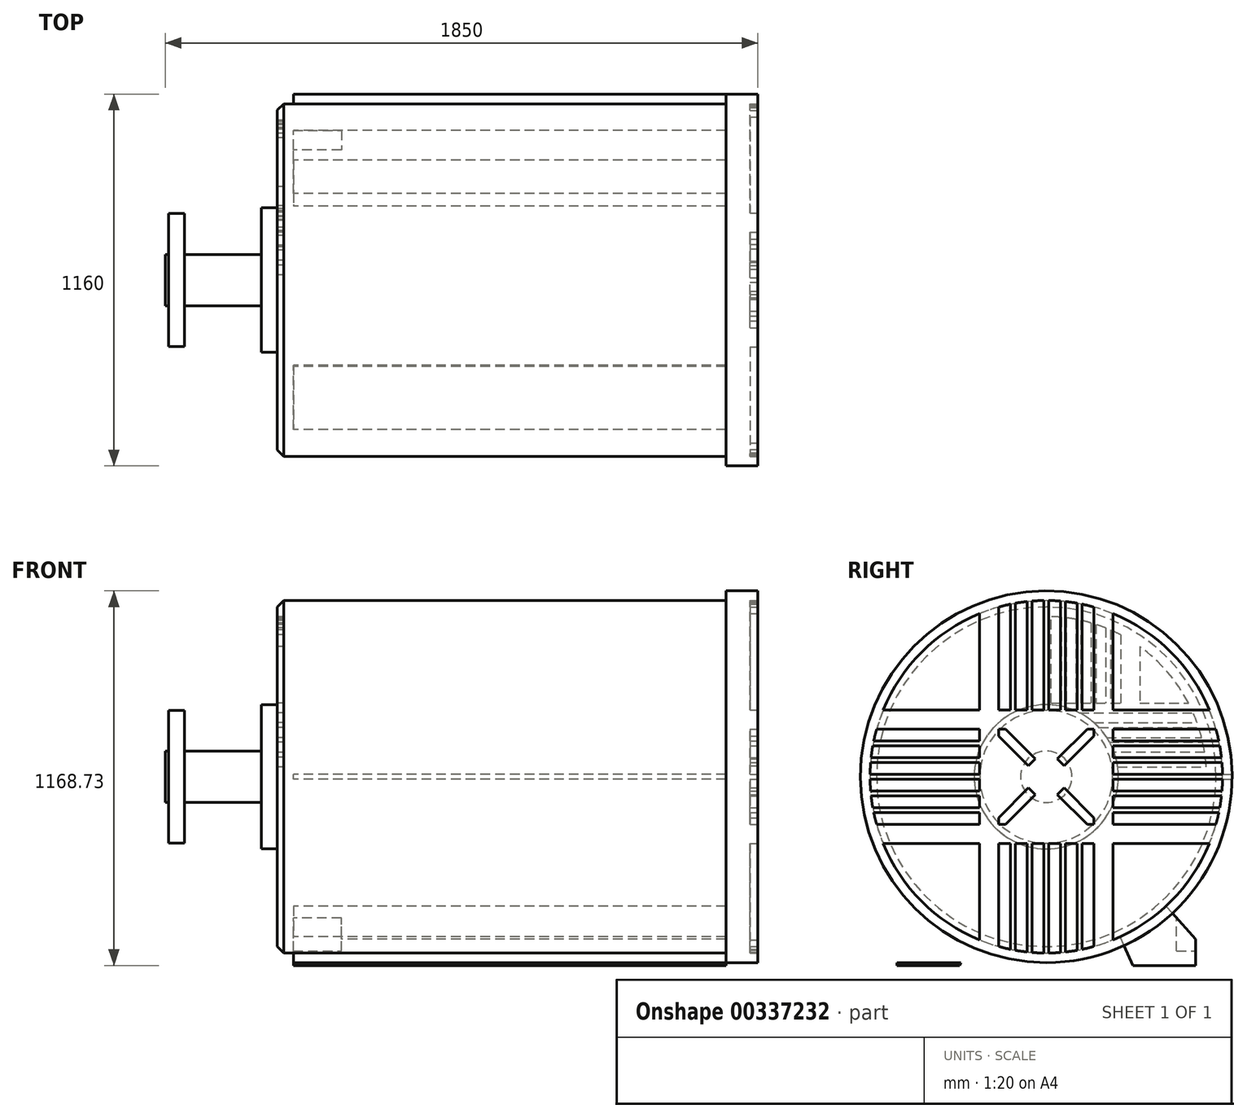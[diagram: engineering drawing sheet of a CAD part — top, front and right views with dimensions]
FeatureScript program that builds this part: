
annotation { "Feature Type Name" : "Feature", "Feature Type Description" : "" }
export const myFeature = defineFeature(function(context is Context, id is Id, definition is map)
    precondition{}
    {
        {
            var Q0;
            Q0=qCreatedBy(makeId("Right.planeOp"),FACE);
            var sketch = newSketch(context, id + "F0", { "sketchPlane" : qUnion([Q0])});
            skCircle(sketch, "E0", {"center": v(0, 0) * mm, "radius": 550 * mm});
            skSolve(sketch);
        }
        {
            var Q0;
            Q0=qSketchRegion(id+"F0",true);
            extrude(context, id + "F1", {"entities" : qUnion([Q0]), "depth" : 1350 * mm});
        }
        {
            var Q0;
            Q0=makeQuery(id+"F1.opExtrude","CAP_FACE",FACE,{"disambiguationData":[OSD([sQuery(id+"F0.wireOp",EDGE,"E0")])],"isStart":true});
            var sketch = newSketch(context, id + "F2", { "sketchPlane" : qUnion([Q0])});
            skLineSegment(sketch, "E1", {"start": v(0, 0) * mm, "end": v(-550, 0) * mm});
            skLineSegment(sketch, "E2", {"start": v(-549.95, 7.5) * mm, "end": v(-579.95, 7.5) * mm});
            skLineSegment(sketch, "E3", {"start": v(-549.95, -7.5) * mm, "end": v(-579.95, -7.5) * mm});
            skLineSegment(sketch, "E4", {"start": v(-549.95, 7.5) * mm, "end": v(-549.95, -7.5) * mm, "construction": true});
            skPoint(sketch, "E5", {"position": v(-549.95, 0) * mm});
            skArc(sketch, "E6", {"start": v(-579.95, 7.5) * mm, "mid": v(-580, 0) * mm, "end": v(-579.95, -7.5) * mm});
            skArc(sketch, "E7", {"start": v(-549.95, 7.5) * mm, "mid": v(-550, 0) * mm, "end": v(-549.95, -7.5) * mm});
            skSolve(sketch);
        }
        {
            var Q0;
            Q0=qSketchRegion(id+"F2",true);
            var Q1;
            Q1=makeQuery(id+"F1.opExtrude","CAP_FACE",FACE,{"disambiguationData":[OSD([sQuery(id+"F0.wireOp",EDGE,"E0")])],"isStart":false});
            extrude(context, id + "F3", {"entities" : qUnion([Q0]), "operationType" : NewBodyOperationType.ADD, "endBound" : BoundingType.UP_TO_SURFACE, "oppositeDirection" : true, "endBoundEntityFace" : qUnion([Q1]), "depth" : 25 * mm});
        }
        {
            var Q0;
            {var subQ0=sQuery(id+"F2.wireOp",EDGE,"E7");var subQ1=sQuery(id+"F2.wireOp",EDGE,"E6");var subQ2=sQuery(id+"F2.wireOp",EDGE,"E3");var subQ3=sQuery(id+"F2.wireOp",EDGE,"E2");Q0=makeQuery(id+"F7dXQ7x4IlYUw1S_1.59.F3.boolean.opBoolean","MERGE",FACE,{"derivedFrom":[makeQuery(id+"F7dXQ7x4IlYUw1S_1.58.F3.boolean.opBoolean","MERGE",FACE,{"derivedFrom":[makeQuery(id+"F7dXQ7x4IlYUw1S_1.57.F3.boolean.opBoolean","MERGE",FACE,{"derivedFrom":[makeQuery(id+"F7dXQ7x4IlYUw1S_1.56.F3.boolean.opBoolean","MERGE",FACE,{"derivedFrom":[makeQuery(id+"F7dXQ7x4IlYUw1S_1.55.F3.boolean.opBoolean","MERGE",FACE,{"derivedFrom":[makeQuery(id+"F7dXQ7x4IlYUw1S_1.54.F3.boolean.opBoolean","MERGE",FACE,{"derivedFrom":[makeQuery(id+"F7dXQ7x4IlYUw1S_1.53.F3.boolean.opBoolean","MERGE",FACE,{"derivedFrom":[makeQuery(id+"F7dXQ7x4IlYUw1S_1.52.F3.boolean.opBoolean","MERGE",FACE,{"derivedFrom":[makeQuery(id+"F7dXQ7x4IlYUw1S_1.51.F3.boolean.opBoolean","MERGE",FACE,{"derivedFrom":[makeQuery(id+"F7dXQ7x4IlYUw1S_1.50.F3.boolean.opBoolean","MERGE",FACE,{"derivedFrom":[makeQuery(id+"F7dXQ7x4IlYUw1S_1.49.F3.boolean.opBoolean","MERGE",FACE,{"derivedFrom":[makeQuery(id+"F7dXQ7x4IlYUw1S_1.48.F3.boolean.opBoolean","MERGE",FACE,{"derivedFrom":[makeQuery(id+"F7dXQ7x4IlYUw1S_1.47.F3.boolean.opBoolean","MERGE",FACE,{"derivedFrom":[makeQuery(id+"F7dXQ7x4IlYUw1S_1.46.F3.boolean.opBoolean","MERGE",FACE,{"derivedFrom":[makeQuery(id+"F7dXQ7x4IlYUw1S_1.45.F3.boolean.opBoolean","MERGE",FACE,{"derivedFrom":[makeQuery(id+"F7dXQ7x4IlYUw1S_1.44.F3.boolean.opBoolean","MERGE",FACE,{"derivedFrom":[makeQuery(id+"F7dXQ7x4IlYUw1S_1.43.F3.boolean.opBoolean","MERGE",FACE,{"derivedFrom":[makeQuery(id+"F7dXQ7x4IlYUw1S_1.42.F3.boolean.opBoolean","MERGE",FACE,{"derivedFrom":[makeQuery(id+"F7dXQ7x4IlYUw1S_1.41.F3.boolean.opBoolean","MERGE",FACE,{"derivedFrom":[makeQuery(id+"F7dXQ7x4IlYUw1S_1.40.F3.boolean.opBoolean","MERGE",FACE,{"derivedFrom":[makeQuery(id+"F7dXQ7x4IlYUw1S_1.39.F3.boolean.opBoolean","MERGE",FACE,{"derivedFrom":[makeQuery(id+"F7dXQ7x4IlYUw1S_1.38.F3.boolean.opBoolean","MERGE",FACE,{"derivedFrom":[makeQuery(id+"F7dXQ7x4IlYUw1S_1.37.F3.boolean.opBoolean","MERGE",FACE,{"derivedFrom":[makeQuery(id+"F7dXQ7x4IlYUw1S_1.36.F3.boolean.opBoolean","MERGE",FACE,{"derivedFrom":[makeQuery(id+"F7dXQ7x4IlYUw1S_1.35.F3.boolean.opBoolean","MERGE",FACE,{"derivedFrom":[makeQuery(id+"F7dXQ7x4IlYUw1S_1.34.F3.boolean.opBoolean","MERGE",FACE,{"derivedFrom":[makeQuery(id+"F7dXQ7x4IlYUw1S_1.33.F3.boolean.opBoolean","MERGE",FACE,{"derivedFrom":[makeQuery(id+"F7dXQ7x4IlYUw1S_1.32.F3.boolean.opBoolean","MERGE",FACE,{"derivedFrom":[makeQuery(id+"F7dXQ7x4IlYUw1S_1.31.F3.boolean.opBoolean","MERGE",FACE,{"derivedFrom":[makeQuery(id+"F7dXQ7x4IlYUw1S_1.30.F3.boolean.opBoolean","MERGE",FACE,{"derivedFrom":[makeQuery(id+"F7dXQ7x4IlYUw1S_1.29.F3.boolean.opBoolean","MERGE",FACE,{"derivedFrom":[makeQuery(id+"F7dXQ7x4IlYUw1S_1.28.F3.boolean.opBoolean","MERGE",FACE,{"derivedFrom":[makeQuery(id+"F7dXQ7x4IlYUw1S_1.27.F3.boolean.opBoolean","MERGE",FACE,{"derivedFrom":[makeQuery(id+"F7dXQ7x4IlYUw1S_1.26.F3.boolean.opBoolean","MERGE",FACE,{"derivedFrom":[makeQuery(id+"F7dXQ7x4IlYUw1S_1.25.F3.boolean.opBoolean","MERGE",FACE,{"derivedFrom":[makeQuery(id+"F7dXQ7x4IlYUw1S_1.24.F3.boolean.opBoolean","MERGE",FACE,{"derivedFrom":[makeQuery(id+"F7dXQ7x4IlYUw1S_1.23.F3.boolean.opBoolean","MERGE",FACE,{"derivedFrom":[makeQuery(id+"F7dXQ7x4IlYUw1S_1.22.F3.boolean.opBoolean","MERGE",FACE,{"derivedFrom":[makeQuery(id+"F7dXQ7x4IlYUw1S_1.21.F3.boolean.opBoolean","MERGE",FACE,{"derivedFrom":[makeQuery(id+"F7dXQ7x4IlYUw1S_1.20.F3.boolean.opBoolean","MERGE",FACE,{"derivedFrom":[makeQuery(id+"F7dXQ7x4IlYUw1S_1.19.F3.boolean.opBoolean","MERGE",FACE,{"derivedFrom":[makeQuery(id+"F7dXQ7x4IlYUw1S_1.18.F3.boolean.opBoolean","MERGE",FACE,{"derivedFrom":[makeQuery(id+"F7dXQ7x4IlYUw1S_1.17.F3.boolean.opBoolean","MERGE",FACE,{"derivedFrom":[makeQuery(id+"F7dXQ7x4IlYUw1S_1.16.F3.boolean.opBoolean","MERGE",FACE,{"derivedFrom":[makeQuery(id+"F7dXQ7x4IlYUw1S_1.15.F3.boolean.opBoolean","MERGE",FACE,{"derivedFrom":[makeQuery(id+"F7dXQ7x4IlYUw1S_1.14.F3.boolean.opBoolean","MERGE",FACE,{"derivedFrom":[makeQuery(id+"F7dXQ7x4IlYUw1S_1.13.F3.boolean.opBoolean","MERGE",FACE,{"derivedFrom":[makeQuery(id+"F7dXQ7x4IlYUw1S_1.12.F3.boolean.opBoolean","MERGE",FACE,{"derivedFrom":[makeQuery(id+"F7dXQ7x4IlYUw1S_1.11.F3.boolean.opBoolean","MERGE",FACE,{"derivedFrom":[makeQuery(id+"F7dXQ7x4IlYUw1S_1.10.F3.boolean.opBoolean","MERGE",FACE,{"derivedFrom":[makeQuery(id+"F7dXQ7x4IlYUw1S_1.9.F3.boolean.opBoolean","MERGE",FACE,{"derivedFrom":[makeQuery(id+"F7dXQ7x4IlYUw1S_1.8.F3.boolean.opBoolean","MERGE",FACE,{"derivedFrom":[makeQuery(id+"F7dXQ7x4IlYUw1S_1.7.F3.boolean.opBoolean","MERGE",FACE,{"derivedFrom":[makeQuery(id+"F7dXQ7x4IlYUw1S_1.6.F3.boolean.opBoolean","MERGE",FACE,{"derivedFrom":[makeQuery(id+"F7dXQ7x4IlYUw1S_1.5.F3.boolean.opBoolean","MERGE",FACE,{"derivedFrom":[makeQuery(id+"F7dXQ7x4IlYUw1S_1.4.F3.boolean.opBoolean","MERGE",FACE,{"derivedFrom":[makeQuery(id+"F7dXQ7x4IlYUw1S_1.3.F3.boolean.opBoolean","MERGE",FACE,{"derivedFrom":[makeQuery(id+"F7dXQ7x4IlYUw1S_1.2.F3.boolean.opBoolean","MERGE",FACE,{"derivedFrom":[makeQuery(id+"F7dXQ7x4IlYUw1S_1.1.F3.boolean.opBoolean","MERGE",FACE,{"derivedFrom":[makeQuery(id+"F3.boolean.opBoolean","MERGE",FACE,{"derivedFrom":[makeQuery(id+"F1.opExtrude","CAP_FACE",FACE,{"disambiguationData":[OSD([sQuery(id+"F0.wireOp",EDGE,"E0")])],"isStart":true}),makeQuery(id+"F3.opExtrude","CAP_FACE",FACE,{"disambiguationData":[OSD([subQ3,subQ2,subQ1,subQ0])],"isStart":true})]}),makeQuery(id+"F7dXQ7x4IlYUw1S_1.1.F3.opExtrude","CAP_FACE",FACE,{"disambiguationData":[OSD([subQ3,subQ2,subQ1,subQ0])],"isStart":true})]}),makeQuery(id+"F7dXQ7x4IlYUw1S_1.2.F3.opExtrude","CAP_FACE",FACE,{"disambiguationData":[OSD([subQ3,subQ2,subQ1,subQ0])],"isStart":true})]}),makeQuery(id+"F7dXQ7x4IlYUw1S_1.3.F3.opExtrude","CAP_FACE",FACE,{"disambiguationData":[OSD([subQ3,subQ2,subQ1,subQ0])],"isStart":true})]}),makeQuery(id+"F7dXQ7x4IlYUw1S_1.4.F3.opExtrude","CAP_FACE",FACE,{"disambiguationData":[OSD([subQ3,subQ2,subQ1,subQ0])],"isStart":true})]}),makeQuery(id+"F7dXQ7x4IlYUw1S_1.5.F3.opExtrude","CAP_FACE",FACE,{"disambiguationData":[OSD([subQ3,subQ2,subQ1,subQ0])],"isStart":true})]}),makeQuery(id+"F7dXQ7x4IlYUw1S_1.6.F3.opExtrude","CAP_FACE",FACE,{"disambiguationData":[OSD([subQ3,subQ2,subQ1,subQ0])],"isStart":true})]}),makeQuery(id+"F7dXQ7x4IlYUw1S_1.7.F3.opExtrude","CAP_FACE",FACE,{"disambiguationData":[OSD([subQ3,subQ2,subQ1,subQ0])],"isStart":true})]}),makeQuery(id+"F7dXQ7x4IlYUw1S_1.8.F3.opExtrude","CAP_FACE",FACE,{"disambiguationData":[OSD([subQ3,subQ2,subQ1,subQ0])],"isStart":true})]}),makeQuery(id+"F7dXQ7x4IlYUw1S_1.9.F3.opExtrude","CAP_FACE",FACE,{"disambiguationData":[OSD([subQ3,subQ2,subQ1,subQ0])],"isStart":true})]}),makeQuery(id+"F7dXQ7x4IlYUw1S_1.10.F3.opExtrude","CAP_FACE",FACE,{"disambiguationData":[OSD([subQ3,subQ2,subQ1,subQ0])],"isStart":true})]}),makeQuery(id+"F7dXQ7x4IlYUw1S_1.11.F3.opExtrude","CAP_FACE",FACE,{"disambiguationData":[OSD([subQ3,subQ2,subQ1,subQ0])],"isStart":true})]}),makeQuery(id+"F7dXQ7x4IlYUw1S_1.12.F3.opExtrude","CAP_FACE",FACE,{"disambiguationData":[OSD([subQ3,subQ2,subQ1,subQ0])],"isStart":true})]}),makeQuery(id+"F7dXQ7x4IlYUw1S_1.13.F3.opExtrude","CAP_FACE",FACE,{"disambiguationData":[OSD([subQ3,subQ2,subQ1,subQ0])],"isStart":true})]}),makeQuery(id+"F7dXQ7x4IlYUw1S_1.14.F3.opExtrude","CAP_FACE",FACE,{"disambiguationData":[OSD([subQ3,subQ2,subQ1,subQ0])],"isStart":true})]}),makeQuery(id+"F7dXQ7x4IlYUw1S_1.15.F3.opExtrude","CAP_FACE",FACE,{"disambiguationData":[OSD([subQ3,subQ2,subQ1,subQ0])],"isStart":true})]}),makeQuery(id+"F7dXQ7x4IlYUw1S_1.16.F3.opExtrude","CAP_FACE",FACE,{"disambiguationData":[OSD([subQ3,subQ2,subQ1,subQ0])],"isStart":true})]}),makeQuery(id+"F7dXQ7x4IlYUw1S_1.17.F3.opExtrude","CAP_FACE",FACE,{"disambiguationData":[OSD([subQ3,subQ2,subQ1,subQ0])],"isStart":true})]}),makeQuery(id+"F7dXQ7x4IlYUw1S_1.18.F3.opExtrude","CAP_FACE",FACE,{"disambiguationData":[OSD([subQ3,subQ2,subQ1,subQ0])],"isStart":true})]}),makeQuery(id+"F7dXQ7x4IlYUw1S_1.19.F3.opExtrude","CAP_FACE",FACE,{"disambiguationData":[OSD([subQ3,subQ2,subQ1,subQ0])],"isStart":true})]}),makeQuery(id+"F7dXQ7x4IlYUw1S_1.20.F3.opExtrude","CAP_FACE",FACE,{"disambiguationData":[OSD([subQ3,subQ2,subQ1,subQ0])],"isStart":true})]}),makeQuery(id+"F7dXQ7x4IlYUw1S_1.21.F3.opExtrude","CAP_FACE",FACE,{"disambiguationData":[OSD([subQ3,subQ2,subQ1,subQ0])],"isStart":true})]}),makeQuery(id+"F7dXQ7x4IlYUw1S_1.22.F3.opExtrude","CAP_FACE",FACE,{"disambiguationData":[OSD([subQ3,subQ2,subQ1,subQ0])],"isStart":true})]}),makeQuery(id+"F7dXQ7x4IlYUw1S_1.23.F3.opExtrude","CAP_FACE",FACE,{"disambiguationData":[OSD([subQ3,subQ2,subQ1,subQ0])],"isStart":true})]}),makeQuery(id+"F7dXQ7x4IlYUw1S_1.24.F3.opExtrude","CAP_FACE",FACE,{"disambiguationData":[OSD([subQ3,subQ2,subQ1,subQ0])],"isStart":true})]}),makeQuery(id+"F7dXQ7x4IlYUw1S_1.25.F3.opExtrude","CAP_FACE",FACE,{"disambiguationData":[OSD([subQ3,subQ2,subQ1,subQ0])],"isStart":true})]}),makeQuery(id+"F7dXQ7x4IlYUw1S_1.26.F3.opExtrude","CAP_FACE",FACE,{"disambiguationData":[OSD([subQ3,subQ2,subQ1,subQ0])],"isStart":true})]}),makeQuery(id+"F7dXQ7x4IlYUw1S_1.27.F3.opExtrude","CAP_FACE",FACE,{"disambiguationData":[OSD([subQ3,subQ2,subQ1,subQ0])],"isStart":true})]}),makeQuery(id+"F7dXQ7x4IlYUw1S_1.28.F3.opExtrude","CAP_FACE",FACE,{"disambiguationData":[OSD([subQ3,subQ2,subQ1,subQ0])],"isStart":true})]}),makeQuery(id+"F7dXQ7x4IlYUw1S_1.29.F3.opExtrude","CAP_FACE",FACE,{"disambiguationData":[OSD([subQ3,subQ2,subQ1,subQ0])],"isStart":true})]}),makeQuery(id+"F7dXQ7x4IlYUw1S_1.30.F3.opExtrude","CAP_FACE",FACE,{"disambiguationData":[OSD([subQ3,subQ2,subQ1,subQ0])],"isStart":true})]}),makeQuery(id+"F7dXQ7x4IlYUw1S_1.31.F3.opExtrude","CAP_FACE",FACE,{"disambiguationData":[OSD([subQ3,subQ2,subQ1,subQ0])],"isStart":true})]}),makeQuery(id+"F7dXQ7x4IlYUw1S_1.32.F3.opExtrude","CAP_FACE",FACE,{"disambiguationData":[OSD([subQ3,subQ2,subQ1,subQ0])],"isStart":true})]}),makeQuery(id+"F7dXQ7x4IlYUw1S_1.33.F3.opExtrude","CAP_FACE",FACE,{"disambiguationData":[OSD([subQ3,subQ2,subQ1,subQ0])],"isStart":true})]}),makeQuery(id+"F7dXQ7x4IlYUw1S_1.34.F3.opExtrude","CAP_FACE",FACE,{"disambiguationData":[OSD([subQ3,subQ2,subQ1,subQ0])],"isStart":true})]}),makeQuery(id+"F7dXQ7x4IlYUw1S_1.35.F3.opExtrude","CAP_FACE",FACE,{"disambiguationData":[OSD([subQ3,subQ2,subQ1,subQ0])],"isStart":true})]}),makeQuery(id+"F7dXQ7x4IlYUw1S_1.36.F3.opExtrude","CAP_FACE",FACE,{"disambiguationData":[OSD([subQ3,subQ2,subQ1,subQ0])],"isStart":true})]}),makeQuery(id+"F7dXQ7x4IlYUw1S_1.37.F3.opExtrude","CAP_FACE",FACE,{"disambiguationData":[OSD([subQ3,subQ2,subQ1,subQ0])],"isStart":true})]}),makeQuery(id+"F7dXQ7x4IlYUw1S_1.38.F3.opExtrude","CAP_FACE",FACE,{"disambiguationData":[OSD([subQ3,subQ2,subQ1,subQ0])],"isStart":true})]}),makeQuery(id+"F7dXQ7x4IlYUw1S_1.39.F3.opExtrude","CAP_FACE",FACE,{"disambiguationData":[OSD([subQ3,subQ2,subQ1,subQ0])],"isStart":true})]}),makeQuery(id+"F7dXQ7x4IlYUw1S_1.40.F3.opExtrude","CAP_FACE",FACE,{"disambiguationData":[OSD([subQ3,subQ2,subQ1,subQ0])],"isStart":true})]}),makeQuery(id+"F7dXQ7x4IlYUw1S_1.41.F3.opExtrude","CAP_FACE",FACE,{"disambiguationData":[OSD([subQ3,subQ2,subQ1,subQ0])],"isStart":true})]}),makeQuery(id+"F7dXQ7x4IlYUw1S_1.42.F3.opExtrude","CAP_FACE",FACE,{"disambiguationData":[OSD([subQ3,subQ2,subQ1,subQ0])],"isStart":true})]}),makeQuery(id+"F7dXQ7x4IlYUw1S_1.43.F3.opExtrude","CAP_FACE",FACE,{"disambiguationData":[OSD([subQ3,subQ2,subQ1,subQ0])],"isStart":true})]}),makeQuery(id+"F7dXQ7x4IlYUw1S_1.44.F3.opExtrude","CAP_FACE",FACE,{"disambiguationData":[OSD([subQ3,subQ2,subQ1,subQ0])],"isStart":true})]}),makeQuery(id+"F7dXQ7x4IlYUw1S_1.45.F3.opExtrude","CAP_FACE",FACE,{"disambiguationData":[OSD([subQ3,subQ2,subQ1,subQ0])],"isStart":true})]}),makeQuery(id+"F7dXQ7x4IlYUw1S_1.46.F3.opExtrude","CAP_FACE",FACE,{"disambiguationData":[OSD([subQ3,subQ2,subQ1,subQ0])],"isStart":true})]}),makeQuery(id+"F7dXQ7x4IlYUw1S_1.47.F3.opExtrude","CAP_FACE",FACE,{"disambiguationData":[OSD([subQ3,subQ2,subQ1,subQ0])],"isStart":true})]}),makeQuery(id+"F7dXQ7x4IlYUw1S_1.48.F3.opExtrude","CAP_FACE",FACE,{"disambiguationData":[OSD([subQ3,subQ2,subQ1,subQ0])],"isStart":true})]}),makeQuery(id+"F7dXQ7x4IlYUw1S_1.49.F3.opExtrude","CAP_FACE",FACE,{"disambiguationData":[OSD([subQ3,subQ2,subQ1,subQ0])],"isStart":true})]}),makeQuery(id+"F7dXQ7x4IlYUw1S_1.50.F3.opExtrude","CAP_FACE",FACE,{"disambiguationData":[OSD([subQ3,subQ2,subQ1,subQ0])],"isStart":true})]}),makeQuery(id+"F7dXQ7x4IlYUw1S_1.51.F3.opExtrude","CAP_FACE",FACE,{"disambiguationData":[OSD([subQ3,subQ2,subQ1,subQ0])],"isStart":true})]}),makeQuery(id+"F7dXQ7x4IlYUw1S_1.52.F3.opExtrude","CAP_FACE",FACE,{"disambiguationData":[OSD([subQ3,subQ2,subQ1,subQ0])],"isStart":true})]}),makeQuery(id+"F7dXQ7x4IlYUw1S_1.53.F3.opExtrude","CAP_FACE",FACE,{"disambiguationData":[OSD([subQ3,subQ2,subQ1,subQ0])],"isStart":true})]}),makeQuery(id+"F7dXQ7x4IlYUw1S_1.54.F3.opExtrude","CAP_FACE",FACE,{"disambiguationData":[OSD([subQ3,subQ2,subQ1,subQ0])],"isStart":true})]}),makeQuery(id+"F7dXQ7x4IlYUw1S_1.55.F3.opExtrude","CAP_FACE",FACE,{"disambiguationData":[OSD([subQ3,subQ2,subQ1,subQ0])],"isStart":true})]}),makeQuery(id+"F7dXQ7x4IlYUw1S_1.56.F3.opExtrude","CAP_FACE",FACE,{"disambiguationData":[OSD([subQ3,subQ2,subQ1,subQ0])],"isStart":true})]}),makeQuery(id+"F7dXQ7x4IlYUw1S_1.57.F3.opExtrude","CAP_FACE",FACE,{"disambiguationData":[OSD([subQ3,subQ2,subQ1,subQ0])],"isStart":true})]}),makeQuery(id+"F7dXQ7x4IlYUw1S_1.58.F3.opExtrude","CAP_FACE",FACE,{"disambiguationData":[OSD([subQ3,subQ2,subQ1,subQ0])],"isStart":true})]}),makeQuery(id+"F7dXQ7x4IlYUw1S_1.59.F3.opExtrude","CAP_FACE",FACE,{"disambiguationData":[OSD([subQ3,subQ2,subQ1,subQ0])],"isStart":true})]});}
            var sketch = newSketch(context, id + "F4", { "sketchPlane" : qUnion([Q0])});
            skCircle(sketch, "E8", {"center": v(0, 0) * mm, "radius": 550 * mm});
            skSolve(sketch);
        }
        {
            var Q0;
            Q0=qSketchRegion(id+"F4",true);
            extrude(context, id + "F5", {"entities" : qUnion([Q0]), "operationType" : NewBodyOperationType.ADD, "depth" : 50 * mm});
        }
        {
            var Q0;
            Q0=makeQuery(id+"F5.opExtrude","CAP_FACE",FACE,{"disambiguationData":[OSD([sQuery(id+"F4.wireOp",EDGE,"E8")])],"isStart":false});
            var sketch = newSketch(context, id + "F6", { "sketchPlane" : qUnion([Q0])});
            skCircle(sketch, "E9", {"center": v(0, 0) * mm, "radius": 225 * mm});
            skSolve(sketch);
        }
        {
            var Q0;
            Q0=qSketchRegion(id+"F6",true);
            extrude(context, id + "F7", {"entities" : qUnion([Q0]), "operationType" : NewBodyOperationType.ADD, "depth" : 50 * mm});
        }
        {
            var Q0;
            Q0=makeQuery(id+"F5.opExtrude","CAP_FACE",FACE,{"disambiguationData":[OSD([sQuery(id+"F4.wireOp",EDGE,"E8")])],"isStart":false});
            var sketch = newSketch(context, id + "F8", { "sketchPlane" : qUnion([Q0])});
            skLineSegment(sketch, "E10", {"start": v(-164.27, 153.75) * mm, "end": v(-475.77, 153.75) * mm});
            skLineSegment(sketch, "E11", {"start": v(-188.73, 122.5) * mm, "end": v(-484.76, 122.5) * mm});
            skLineSegment(sketch, "E12", {"start": v(-216.5, 61.25) * mm, "end": v(-496.23, 61.25) * mm});
            skLineSegment(sketch, "E13", {"start": v(-223, 30) * mm, "end": v(-499.1, 30) * mm});
            skArc(sketch, "E14", {"start": v(-164.27, 153.75) * mm, "mid": v(-177.2, 138.67) * mm, "end": v(-188.73, 122.5) * mm});
            skArc(sketch, "E15", {"start": v(-216.5, 61.25) * mm, "mid": v(-220.3, 45.74) * mm, "end": v(-223, 30) * mm});
            skLineSegment(sketch, "E16", {"start": v(-197.66, 107.5) * mm, "end": v(-488.3, 107.5) * mm});
            skLineSegment(sketch, "E17", {"start": v(-494.15, 76.25) * mm, "end": v(-211.69, 76.25) * mm});
            skArc(sketch, "E18", {"start": v(-197.66, 107.5) * mm, "mid": v(-205.27, 92.14) * mm, "end": v(-211.69, 76.25) * mm});
            skLineSegment(sketch, "E19", {"start": v(-103.08, 200) * mm, "end": v(-458.26, 200) * mm});
            skLineSegment(sketch, "E20", {"start": v(-148.82, 168.75) * mm, "end": v(-470.66, 168.75) * mm});
            skArc(sketch, "E21", {"start": v(-103.08, 200) * mm, "mid": v(-126.92, 185.79) * mm, "end": v(-148.82, 168.75) * mm});
            skLineSegment(sketch, "E22", {"start": v(-220.07, 30) * mm, "end": v(-220.07, 61.25) * mm, "construction": true});
            skLineSegment(sketch, "E23", {"start": v(-100.58, 76.25) * mm, "end": v(-100.58, 107.5) * mm, "construction": true});
            skLineSegment(sketch, "E24", {"start": v(-97.25, 122.5) * mm, "end": v(-97.25, 153.75) * mm, "construction": true});
            skLineSegment(sketch, "E25", {"start": v(-67, 168.75) * mm, "end": v(-67, 200) * mm, "construction": true});
            skArc(sketch, "E26", {"start": v(-458.26, 200) * mm, "mid": v(-464.72, 184.48) * mm, "end": v(-470.66, 168.75) * mm});
            skArc(sketch, "E27.trimOffspring", {"start": v(-496.23, 61.25) * mm, "mid": v(-497.91, 45.65) * mm, "end": v(-499.1, 30) * mm});
            skArc(sketch, "E28.trimOffspring", {"start": v(-488.3, 107.5) * mm, "mid": v(-491.48, 91.92) * mm, "end": v(-494.15, 76.25) * mm});
            skArc(sketch, "E29.trimOffspring", {"start": v(-475.77, 153.75) * mm, "mid": v(-480.52, 138.2) * mm, "end": v(-484.76, 122.5) * mm});
            skSolve(sketch);
        }
        {
            var Q0;
            Q0=qSketchRegion(id+"F8",true);
            extrude(context, id + "F9", {"entities" : qUnion([Q0]), "operationType" : NewBodyOperationType.REMOVE, "oppositeDirection" : true, "depth" : 20 * mm});
        }
        {
            var Q0;
            Q0=makeQuery(id+"F5.opExtrude","CAP_FACE",FACE,{"disambiguationData":[OSD([sQuery(id+"F4.wireOp",EDGE,"E8")])],"isStart":false});
            var sketch = newSketch(context, id + "F10", { "sketchPlane" : qUnion([Q0])});
            skLineSegment(sketch, "E30", {"start": v(-15.63, 230) * mm, "end": v(-15.63, 499.76) * mm});
            skLineSegment(sketch, "E31", {"start": v(-46.88, 497.8) * mm, "end": v(-46.88, 230) * mm});
            skLineSegment(sketch, "E32", {"start": v(-61.88, 496.16) * mm, "end": v(-61.88, 230) * mm});
            skLineSegment(sketch, "E33", {"start": v(-93.13, 491.25) * mm, "end": v(-93.13, 230) * mm});
            skLineSegment(sketch, "E34", {"start": v(-108.13, 488.17) * mm, "end": v(-108.13, 230) * mm});
            skLineSegment(sketch, "E35", {"start": v(-139.38, 480.18) * mm, "end": v(-139.38, 230) * mm});
            skLineSegment(sketch, "E36", {"start": v(-154.38, 475.57) * mm, "end": v(-154.38, 230) * mm});
            skLineSegment(sketch, "E37", {"start": v(-185.63, 464.27) * mm, "end": v(-185.63, 230) * mm});
            skLineSegment(sketch, "E38", {"start": v(-200.63, 457.98) * mm, "end": v(-200.63, 230) * mm});
            skLineSegment(sketch, "E39", {"start": v(-231.88, 442.98) * mm, "end": v(-231.88, 230) * mm});
            skLineSegment(sketch, "E40", {"start": v(-15.63, 230) * mm, "end": v(-46.88, 230) * mm});
            skLineSegment(sketch, "E41", {"start": v(-231.88, 184.58) * mm, "end": v(-200.63, 184.58) * mm, "construction": true});
            skLineSegment(sketch, "E42", {"start": v(-185.63, 198.94) * mm, "end": v(-154.38, 198.94) * mm, "construction": true});
            skLineSegment(sketch, "E43", {"start": v(-139.38, 197.69) * mm, "end": v(-108.13, 197.69) * mm, "construction": true});
            skLineSegment(sketch, "E44", {"start": v(-93.13, 203.42) * mm, "end": v(-61.88, 203.42) * mm, "construction": true});
            skLineSegment(sketch, "E45", {"start": v(-46.88, 212.68) * mm, "end": v(-15.63, 212.68) * mm, "construction": true});
            skArc(sketch, "E46", {"start": v(-15.63, 499.76) * mm, "mid": v(-31.27, 499.02) * mm, "end": v(-46.88, 497.8) * mm});
            skLineSegment(sketch, "E47.trimOffspring", {"start": v(-61.88, 230) * mm, "end": v(-93.13, 230) * mm});
            skLineSegment(sketch, "E48.trimOffspring", {"start": v(-108.13, 230) * mm, "end": v(-139.38, 230) * mm});
            skLineSegment(sketch, "E49.trimOffspring", {"start": v(-154.38, 230) * mm, "end": v(-185.63, 230) * mm});
            skLineSegment(sketch, "E50.trimOffspring", {"start": v(-200.63, 230) * mm, "end": v(-231.88, 230) * mm});
            skArc(sketch, "E51.trimOffspring", {"start": v(-200.63, 457.98) * mm, "mid": v(-216.38, 450.75) * mm, "end": v(-231.88, 442.98) * mm});
            skArc(sketch, "E52.trimOffspring", {"start": v(-154.38, 475.57) * mm, "mid": v(-170.1, 470.18) * mm, "end": v(-185.63, 464.27) * mm});
            skArc(sketch, "E53.trimOffspring", {"start": v(-108.13, 488.17) * mm, "mid": v(-123.81, 484.43) * mm, "end": v(-139.38, 480.18) * mm});
            skArc(sketch, "E54.trimOffspring", {"start": v(-61.88, 496.16) * mm, "mid": v(-77.54, 493.95) * mm, "end": v(-93.13, 491.25) * mm});
            skArc(sketch, "E55", {"start": v(-291.88, 405.97) * mm, "mid": v(-378.3, 326.95) * mm, "end": v(-443.96, 230) * mm});
            skLineSegment(sketch, "E56", {"start": v(-291.88, 405.97) * mm, "end": v(-291.88, 230) * mm});
            skLineSegment(sketch, "E57", {"start": v(-291.88, 230) * mm, "end": v(-443.96, 230) * mm});
            skSolve(sketch);
        }
        {
            var Q0;
            Q0=qSketchRegion(id+"F10",true);
            var Q1;
            Q1=makeQuery(id+"F9.boolean.opBoolean","COPY",FACE,{"derivedFrom":makeQuery(id+"F9.opExtrude","CAP_FACE",FACE,{"disambiguationData":[OSD([sQuery(id+"F8.wireOp",EDGE,"E19"),sQuery(id+"F8.wireOp",EDGE,"E20"),sQuery(id+"F8.wireOp",EDGE,"E21"),sQuery(id+"F8.wireOp",EDGE,"E26")])],"isStart":false})});
            extrude(context, id + "F11", {"entities" : qUnion([Q0]), "operationType" : NewBodyOperationType.REMOVE, "endBound" : BoundingType.UP_TO_SURFACE, "oppositeDirection" : true, "endBoundEntityFace" : qUnion([Q1]), "depth" : 25 * mm});
        }
        {
            var Q0;
            {var subQ0=sQuery(id+"F2.wireOp",EDGE,"E6");var subQ1=sQuery(id+"F2.wireOp",EDGE,"E3");var subQ2=sQuery(id+"F2.wireOp",EDGE,"E2");var subQ3=sQuery(id+"F0.wireOp",EDGE,"E0");var subQ4=sQuery(id+"F2.wireOp",EDGE,"E7");Q0=makeQuery(id+"F5.boolean.opBoolean","SPLIT",FACE,{"disambiguationData":[TD([makeQuery(id+"F7dXQ7x4IlYUw1S_1.56.F3.opExtrude","SWEPT_FACE",FACE,{"disambiguationData":[OSD([subQ2])]})])],"derivedFrom":makeQuery(id+"F7dXQ7x4IlYUw1S_1.59.F3.boolean.opBoolean","MERGE",FACE,{"derivedFrom":[makeQuery(id+"F7dXQ7x4IlYUw1S_1.58.F3.boolean.opBoolean","MERGE",FACE,{"derivedFrom":[makeQuery(id+"F7dXQ7x4IlYUw1S_1.57.F3.boolean.opBoolean","MERGE",FACE,{"derivedFrom":[makeQuery(id+"F7dXQ7x4IlYUw1S_1.56.F3.boolean.opBoolean","MERGE",FACE,{"derivedFrom":[makeQuery(id+"F7dXQ7x4IlYUw1S_1.55.F3.boolean.opBoolean","MERGE",FACE,{"derivedFrom":[makeQuery(id+"F7dXQ7x4IlYUw1S_1.54.F3.boolean.opBoolean","MERGE",FACE,{"derivedFrom":[makeQuery(id+"F7dXQ7x4IlYUw1S_1.53.F3.boolean.opBoolean","MERGE",FACE,{"derivedFrom":[makeQuery(id+"F7dXQ7x4IlYUw1S_1.52.F3.boolean.opBoolean","MERGE",FACE,{"derivedFrom":[makeQuery(id+"F7dXQ7x4IlYUw1S_1.51.F3.boolean.opBoolean","MERGE",FACE,{"derivedFrom":[makeQuery(id+"F7dXQ7x4IlYUw1S_1.50.F3.boolean.opBoolean","MERGE",FACE,{"derivedFrom":[makeQuery(id+"F7dXQ7x4IlYUw1S_1.49.F3.boolean.opBoolean","MERGE",FACE,{"derivedFrom":[makeQuery(id+"F7dXQ7x4IlYUw1S_1.48.F3.boolean.opBoolean","MERGE",FACE,{"derivedFrom":[makeQuery(id+"F7dXQ7x4IlYUw1S_1.47.F3.boolean.opBoolean","MERGE",FACE,{"derivedFrom":[makeQuery(id+"F7dXQ7x4IlYUw1S_1.46.F3.boolean.opBoolean","MERGE",FACE,{"derivedFrom":[makeQuery(id+"F7dXQ7x4IlYUw1S_1.45.F3.boolean.opBoolean","MERGE",FACE,{"derivedFrom":[makeQuery(id+"F7dXQ7x4IlYUw1S_1.44.F3.boolean.opBoolean","MERGE",FACE,{"derivedFrom":[makeQuery(id+"F7dXQ7x4IlYUw1S_1.43.F3.boolean.opBoolean","MERGE",FACE,{"derivedFrom":[makeQuery(id+"F7dXQ7x4IlYUw1S_1.42.F3.boolean.opBoolean","MERGE",FACE,{"derivedFrom":[makeQuery(id+"F7dXQ7x4IlYUw1S_1.41.F3.boolean.opBoolean","MERGE",FACE,{"derivedFrom":[makeQuery(id+"F7dXQ7x4IlYUw1S_1.40.F3.boolean.opBoolean","MERGE",FACE,{"derivedFrom":[makeQuery(id+"F7dXQ7x4IlYUw1S_1.39.F3.boolean.opBoolean","MERGE",FACE,{"derivedFrom":[makeQuery(id+"F7dXQ7x4IlYUw1S_1.38.F3.boolean.opBoolean","MERGE",FACE,{"derivedFrom":[makeQuery(id+"F7dXQ7x4IlYUw1S_1.37.F3.boolean.opBoolean","MERGE",FACE,{"derivedFrom":[makeQuery(id+"F7dXQ7x4IlYUw1S_1.36.F3.boolean.opBoolean","MERGE",FACE,{"derivedFrom":[makeQuery(id+"F7dXQ7x4IlYUw1S_1.35.F3.boolean.opBoolean","MERGE",FACE,{"derivedFrom":[makeQuery(id+"F7dXQ7x4IlYUw1S_1.34.F3.boolean.opBoolean","MERGE",FACE,{"derivedFrom":[makeQuery(id+"F7dXQ7x4IlYUw1S_1.33.F3.boolean.opBoolean","MERGE",FACE,{"derivedFrom":[makeQuery(id+"F7dXQ7x4IlYUw1S_1.32.F3.boolean.opBoolean","MERGE",FACE,{"derivedFrom":[makeQuery(id+"F7dXQ7x4IlYUw1S_1.31.F3.boolean.opBoolean","MERGE",FACE,{"derivedFrom":[makeQuery(id+"F7dXQ7x4IlYUw1S_1.30.F3.boolean.opBoolean","MERGE",FACE,{"derivedFrom":[makeQuery(id+"F7dXQ7x4IlYUw1S_1.29.F3.boolean.opBoolean","MERGE",FACE,{"derivedFrom":[makeQuery(id+"F7dXQ7x4IlYUw1S_1.28.F3.boolean.opBoolean","MERGE",FACE,{"derivedFrom":[makeQuery(id+"F7dXQ7x4IlYUw1S_1.27.F3.boolean.opBoolean","MERGE",FACE,{"derivedFrom":[makeQuery(id+"F7dXQ7x4IlYUw1S_1.26.F3.boolean.opBoolean","MERGE",FACE,{"derivedFrom":[makeQuery(id+"F7dXQ7x4IlYUw1S_1.25.F3.boolean.opBoolean","MERGE",FACE,{"derivedFrom":[makeQuery(id+"F7dXQ7x4IlYUw1S_1.24.F3.boolean.opBoolean","MERGE",FACE,{"derivedFrom":[makeQuery(id+"F7dXQ7x4IlYUw1S_1.23.F3.boolean.opBoolean","MERGE",FACE,{"derivedFrom":[makeQuery(id+"F7dXQ7x4IlYUw1S_1.22.F3.boolean.opBoolean","MERGE",FACE,{"derivedFrom":[makeQuery(id+"F7dXQ7x4IlYUw1S_1.21.F3.boolean.opBoolean","MERGE",FACE,{"derivedFrom":[makeQuery(id+"F7dXQ7x4IlYUw1S_1.20.F3.boolean.opBoolean","MERGE",FACE,{"derivedFrom":[makeQuery(id+"F7dXQ7x4IlYUw1S_1.19.F3.boolean.opBoolean","MERGE",FACE,{"derivedFrom":[makeQuery(id+"F7dXQ7x4IlYUw1S_1.18.F3.boolean.opBoolean","MERGE",FACE,{"derivedFrom":[makeQuery(id+"F7dXQ7x4IlYUw1S_1.17.F3.boolean.opBoolean","MERGE",FACE,{"derivedFrom":[makeQuery(id+"F7dXQ7x4IlYUw1S_1.16.F3.boolean.opBoolean","MERGE",FACE,{"derivedFrom":[makeQuery(id+"F7dXQ7x4IlYUw1S_1.15.F3.boolean.opBoolean","MERGE",FACE,{"derivedFrom":[makeQuery(id+"F7dXQ7x4IlYUw1S_1.14.F3.boolean.opBoolean","MERGE",FACE,{"derivedFrom":[makeQuery(id+"F7dXQ7x4IlYUw1S_1.13.F3.boolean.opBoolean","MERGE",FACE,{"derivedFrom":[makeQuery(id+"F7dXQ7x4IlYUw1S_1.12.F3.boolean.opBoolean","MERGE",FACE,{"derivedFrom":[makeQuery(id+"F7dXQ7x4IlYUw1S_1.11.F3.boolean.opBoolean","MERGE",FACE,{"derivedFrom":[makeQuery(id+"F7dXQ7x4IlYUw1S_1.10.F3.boolean.opBoolean","MERGE",FACE,{"derivedFrom":[makeQuery(id+"F7dXQ7x4IlYUw1S_1.9.F3.boolean.opBoolean","MERGE",FACE,{"derivedFrom":[makeQuery(id+"F7dXQ7x4IlYUw1S_1.8.F3.boolean.opBoolean","MERGE",FACE,{"derivedFrom":[makeQuery(id+"F7dXQ7x4IlYUw1S_1.7.F3.boolean.opBoolean","MERGE",FACE,{"derivedFrom":[makeQuery(id+"F7dXQ7x4IlYUw1S_1.6.F3.boolean.opBoolean","MERGE",FACE,{"derivedFrom":[makeQuery(id+"F7dXQ7x4IlYUw1S_1.5.F3.boolean.opBoolean","MERGE",FACE,{"derivedFrom":[makeQuery(id+"F7dXQ7x4IlYUw1S_1.4.F3.boolean.opBoolean","MERGE",FACE,{"derivedFrom":[makeQuery(id+"F7dXQ7x4IlYUw1S_1.3.F3.boolean.opBoolean","MERGE",FACE,{"derivedFrom":[makeQuery(id+"F7dXQ7x4IlYUw1S_1.2.F3.boolean.opBoolean","MERGE",FACE,{"derivedFrom":[makeQuery(id+"F7dXQ7x4IlYUw1S_1.1.F3.boolean.opBoolean","MERGE",FACE,{"derivedFrom":[makeQuery(id+"F3.boolean.opBoolean","MERGE",FACE,{"derivedFrom":[makeQuery(id+"F1.opExtrude","CAP_FACE",FACE,{"disambiguationData":[OSD([subQ3])],"isStart":true}),makeQuery(id+"F3.opExtrude","CAP_FACE",FACE,{"disambiguationData":[OSD([subQ2,subQ1,subQ0,subQ4])],"isStart":true})]}),makeQuery(id+"F7dXQ7x4IlYUw1S_1.1.F3.opExtrude","CAP_FACE",FACE,{"disambiguationData":[OSD([subQ2,subQ1,subQ0,subQ4])],"isStart":true})]}),makeQuery(id+"F7dXQ7x4IlYUw1S_1.2.F3.opExtrude","CAP_FACE",FACE,{"disambiguationData":[OSD([subQ2,subQ1,subQ0,subQ4])],"isStart":true})]}),makeQuery(id+"F7dXQ7x4IlYUw1S_1.3.F3.opExtrude","CAP_FACE",FACE,{"disambiguationData":[OSD([subQ2,subQ1,subQ0,subQ4])],"isStart":true})]}),makeQuery(id+"F7dXQ7x4IlYUw1S_1.4.F3.opExtrude","CAP_FACE",FACE,{"disambiguationData":[OSD([subQ2,subQ1,subQ0,subQ4])],"isStart":true})]}),makeQuery(id+"F7dXQ7x4IlYUw1S_1.5.F3.opExtrude","CAP_FACE",FACE,{"disambiguationData":[OSD([subQ2,subQ1,subQ0,subQ4])],"isStart":true})]}),makeQuery(id+"F7dXQ7x4IlYUw1S_1.6.F3.opExtrude","CAP_FACE",FACE,{"disambiguationData":[OSD([subQ2,subQ1,subQ0,subQ4])],"isStart":true})]}),makeQuery(id+"F7dXQ7x4IlYUw1S_1.7.F3.opExtrude","CAP_FACE",FACE,{"disambiguationData":[OSD([subQ2,subQ1,subQ0,subQ4])],"isStart":true})]}),makeQuery(id+"F7dXQ7x4IlYUw1S_1.8.F3.opExtrude","CAP_FACE",FACE,{"disambiguationData":[OSD([subQ2,subQ1,subQ0,subQ4])],"isStart":true})]}),makeQuery(id+"F7dXQ7x4IlYUw1S_1.9.F3.opExtrude","CAP_FACE",FACE,{"disambiguationData":[OSD([subQ2,subQ1,subQ0,subQ4])],"isStart":true})]}),makeQuery(id+"F7dXQ7x4IlYUw1S_1.10.F3.opExtrude","CAP_FACE",FACE,{"disambiguationData":[OSD([subQ2,subQ1,subQ0,subQ4])],"isStart":true})]}),makeQuery(id+"F7dXQ7x4IlYUw1S_1.11.F3.opExtrude","CAP_FACE",FACE,{"disambiguationData":[OSD([subQ2,subQ1,subQ0,subQ4])],"isStart":true})]}),makeQuery(id+"F7dXQ7x4IlYUw1S_1.12.F3.opExtrude","CAP_FACE",FACE,{"disambiguationData":[OSD([subQ2,subQ1,subQ0,subQ4])],"isStart":true})]}),makeQuery(id+"F7dXQ7x4IlYUw1S_1.13.F3.opExtrude","CAP_FACE",FACE,{"disambiguationData":[OSD([subQ2,subQ1,subQ0,subQ4])],"isStart":true})]}),makeQuery(id+"F7dXQ7x4IlYUw1S_1.14.F3.opExtrude","CAP_FACE",FACE,{"disambiguationData":[OSD([subQ2,subQ1,subQ0,subQ4])],"isStart":true})]}),makeQuery(id+"F7dXQ7x4IlYUw1S_1.15.F3.opExtrude","CAP_FACE",FACE,{"disambiguationData":[OSD([subQ2,subQ1,subQ0,subQ4])],"isStart":true})]}),makeQuery(id+"F7dXQ7x4IlYUw1S_1.16.F3.opExtrude","CAP_FACE",FACE,{"disambiguationData":[OSD([subQ2,subQ1,subQ0,subQ4])],"isStart":true})]}),makeQuery(id+"F7dXQ7x4IlYUw1S_1.17.F3.opExtrude","CAP_FACE",FACE,{"disambiguationData":[OSD([subQ2,subQ1,subQ0,subQ4])],"isStart":true})]}),makeQuery(id+"F7dXQ7x4IlYUw1S_1.18.F3.opExtrude","CAP_FACE",FACE,{"disambiguationData":[OSD([subQ2,subQ1,subQ0,subQ4])],"isStart":true})]}),makeQuery(id+"F7dXQ7x4IlYUw1S_1.19.F3.opExtrude","CAP_FACE",FACE,{"disambiguationData":[OSD([subQ2,subQ1,subQ0,subQ4])],"isStart":true})]}),makeQuery(id+"F7dXQ7x4IlYUw1S_1.20.F3.opExtrude","CAP_FACE",FACE,{"disambiguationData":[OSD([subQ2,subQ1,subQ0,subQ4])],"isStart":true})]}),makeQuery(id+"F7dXQ7x4IlYUw1S_1.21.F3.opExtrude","CAP_FACE",FACE,{"disambiguationData":[OSD([subQ2,subQ1,subQ0,subQ4])],"isStart":true})]}),makeQuery(id+"F7dXQ7x4IlYUw1S_1.22.F3.opExtrude","CAP_FACE",FACE,{"disambiguationData":[OSD([subQ2,subQ1,subQ0,subQ4])],"isStart":true})]}),makeQuery(id+"F7dXQ7x4IlYUw1S_1.23.F3.opExtrude","CAP_FACE",FACE,{"disambiguationData":[OSD([subQ2,subQ1,subQ0,subQ4])],"isStart":true})]}),makeQuery(id+"F7dXQ7x4IlYUw1S_1.24.F3.opExtrude","CAP_FACE",FACE,{"disambiguationData":[OSD([subQ2,subQ1,subQ0,subQ4])],"isStart":true})]}),makeQuery(id+"F7dXQ7x4IlYUw1S_1.25.F3.opExtrude","CAP_FACE",FACE,{"disambiguationData":[OSD([subQ2,subQ1,subQ0,subQ4])],"isStart":true})]}),makeQuery(id+"F7dXQ7x4IlYUw1S_1.26.F3.opExtrude","CAP_FACE",FACE,{"disambiguationData":[OSD([subQ2,subQ1,subQ0,subQ4])],"isStart":true})]}),makeQuery(id+"F7dXQ7x4IlYUw1S_1.27.F3.opExtrude","CAP_FACE",FACE,{"disambiguationData":[OSD([subQ2,subQ1,subQ0,subQ4])],"isStart":true})]}),makeQuery(id+"F7dXQ7x4IlYUw1S_1.28.F3.opExtrude","CAP_FACE",FACE,{"disambiguationData":[OSD([subQ2,subQ1,subQ0,subQ4])],"isStart":true})]}),makeQuery(id+"F7dXQ7x4IlYUw1S_1.29.F3.opExtrude","CAP_FACE",FACE,{"disambiguationData":[OSD([subQ2,subQ1,subQ0,subQ4])],"isStart":true})]}),makeQuery(id+"F7dXQ7x4IlYUw1S_1.30.F3.opExtrude","CAP_FACE",FACE,{"disambiguationData":[OSD([subQ2,subQ1,subQ0,subQ4])],"isStart":true})]}),makeQuery(id+"F7dXQ7x4IlYUw1S_1.31.F3.opExtrude","CAP_FACE",FACE,{"disambiguationData":[OSD([subQ2,subQ1,subQ0,subQ4])],"isStart":true})]}),makeQuery(id+"F7dXQ7x4IlYUw1S_1.32.F3.opExtrude","CAP_FACE",FACE,{"disambiguationData":[OSD([subQ2,subQ1,subQ0,subQ4])],"isStart":true})]}),makeQuery(id+"F7dXQ7x4IlYUw1S_1.33.F3.opExtrude","CAP_FACE",FACE,{"disambiguationData":[OSD([subQ2,subQ1,subQ0,subQ4])],"isStart":true})]}),makeQuery(id+"F7dXQ7x4IlYUw1S_1.34.F3.opExtrude","CAP_FACE",FACE,{"disambiguationData":[OSD([subQ2,subQ1,subQ0,subQ4])],"isStart":true})]}),makeQuery(id+"F7dXQ7x4IlYUw1S_1.35.F3.opExtrude","CAP_FACE",FACE,{"disambiguationData":[OSD([subQ2,subQ1,subQ0,subQ4])],"isStart":true})]}),makeQuery(id+"F7dXQ7x4IlYUw1S_1.36.F3.opExtrude","CAP_FACE",FACE,{"disambiguationData":[OSD([subQ2,subQ1,subQ0,subQ4])],"isStart":true})]}),makeQuery(id+"F7dXQ7x4IlYUw1S_1.37.F3.opExtrude","CAP_FACE",FACE,{"disambiguationData":[OSD([subQ2,subQ1,subQ0,subQ4])],"isStart":true})]}),makeQuery(id+"F7dXQ7x4IlYUw1S_1.38.F3.opExtrude","CAP_FACE",FACE,{"disambiguationData":[OSD([subQ2,subQ1,subQ0,subQ4])],"isStart":true})]}),makeQuery(id+"F7dXQ7x4IlYUw1S_1.39.F3.opExtrude","CAP_FACE",FACE,{"disambiguationData":[OSD([subQ2,subQ1,subQ0,subQ4])],"isStart":true})]}),makeQuery(id+"F7dXQ7x4IlYUw1S_1.40.F3.opExtrude","CAP_FACE",FACE,{"disambiguationData":[OSD([subQ2,subQ1,subQ0,subQ4])],"isStart":true})]}),makeQuery(id+"F7dXQ7x4IlYUw1S_1.41.F3.opExtrude","CAP_FACE",FACE,{"disambiguationData":[OSD([subQ2,subQ1,subQ0,subQ4])],"isStart":true})]}),makeQuery(id+"F7dXQ7x4IlYUw1S_1.42.F3.opExtrude","CAP_FACE",FACE,{"disambiguationData":[OSD([subQ2,subQ1,subQ0,subQ4])],"isStart":true})]}),makeQuery(id+"F7dXQ7x4IlYUw1S_1.43.F3.opExtrude","CAP_FACE",FACE,{"disambiguationData":[OSD([subQ2,subQ1,subQ0,subQ4])],"isStart":true})]}),makeQuery(id+"F7dXQ7x4IlYUw1S_1.44.F3.opExtrude","CAP_FACE",FACE,{"disambiguationData":[OSD([subQ2,subQ1,subQ0,subQ4])],"isStart":true})]}),makeQuery(id+"F7dXQ7x4IlYUw1S_1.45.F3.opExtrude","CAP_FACE",FACE,{"disambiguationData":[OSD([subQ2,subQ1,subQ0,subQ4])],"isStart":true})]}),makeQuery(id+"F7dXQ7x4IlYUw1S_1.46.F3.opExtrude","CAP_FACE",FACE,{"disambiguationData":[OSD([subQ2,subQ1,subQ0,subQ4])],"isStart":true})]}),makeQuery(id+"F7dXQ7x4IlYUw1S_1.47.F3.opExtrude","CAP_FACE",FACE,{"disambiguationData":[OSD([subQ2,subQ1,subQ0,subQ4])],"isStart":true})]}),makeQuery(id+"F7dXQ7x4IlYUw1S_1.48.F3.opExtrude","CAP_FACE",FACE,{"disambiguationData":[OSD([subQ2,subQ1,subQ0,subQ4])],"isStart":true})]}),makeQuery(id+"F7dXQ7x4IlYUw1S_1.49.F3.opExtrude","CAP_FACE",FACE,{"disambiguationData":[OSD([subQ2,subQ1,subQ0,subQ4])],"isStart":true})]}),makeQuery(id+"F7dXQ7x4IlYUw1S_1.50.F3.opExtrude","CAP_FACE",FACE,{"disambiguationData":[OSD([subQ2,subQ1,subQ0,subQ4])],"isStart":true})]}),makeQuery(id+"F7dXQ7x4IlYUw1S_1.51.F3.opExtrude","CAP_FACE",FACE,{"disambiguationData":[OSD([subQ2,subQ1,subQ0,subQ4])],"isStart":true})]}),makeQuery(id+"F7dXQ7x4IlYUw1S_1.52.F3.opExtrude","CAP_FACE",FACE,{"disambiguationData":[OSD([subQ2,subQ1,subQ0,subQ4])],"isStart":true})]}),makeQuery(id+"F7dXQ7x4IlYUw1S_1.53.F3.opExtrude","CAP_FACE",FACE,{"disambiguationData":[OSD([subQ2,subQ1,subQ0,subQ4])],"isStart":true})]}),makeQuery(id+"F7dXQ7x4IlYUw1S_1.54.F3.opExtrude","CAP_FACE",FACE,{"disambiguationData":[OSD([subQ2,subQ1,subQ0,subQ4])],"isStart":true})]}),makeQuery(id+"F7dXQ7x4IlYUw1S_1.55.F3.opExtrude","CAP_FACE",FACE,{"disambiguationData":[OSD([subQ2,subQ1,subQ0,subQ4])],"isStart":true})]}),makeQuery(id+"F7dXQ7x4IlYUw1S_1.56.F3.opExtrude","CAP_FACE",FACE,{"disambiguationData":[OSD([subQ2,subQ1,subQ0,subQ4])],"isStart":true})]}),makeQuery(id+"F7dXQ7x4IlYUw1S_1.57.F3.opExtrude","CAP_FACE",FACE,{"disambiguationData":[OSD([subQ2,subQ1,subQ0,subQ4])],"isStart":true})]}),makeQuery(id+"F7dXQ7x4IlYUw1S_1.58.F3.opExtrude","CAP_FACE",FACE,{"disambiguationData":[OSD([subQ2,subQ1,subQ0,subQ4])],"isStart":true})]}),makeQuery(id+"F7dXQ7x4IlYUw1S_1.59.F3.opExtrude","CAP_FACE",FACE,{"disambiguationData":[OSD([subQ2,subQ1,subQ0,subQ4])],"isStart":true})]})});}
            var Q1;
            {var subQ0=sQuery(id+"F2.wireOp",EDGE,"E7");var subQ1=sQuery(id+"F2.wireOp",EDGE,"E6");var subQ2=sQuery(id+"F2.wireOp",EDGE,"E3");var subQ3=sQuery(id+"F2.wireOp",EDGE,"E2");Q1=makeQuery(id+"F7dXQ7x4IlYUw1S_1.59.F3.boolean.opBoolean","MERGE",FACE,{"derivedFrom":[makeQuery(id+"F7dXQ7x4IlYUw1S_1.58.F3.boolean.opBoolean","MERGE",FACE,{"derivedFrom":[makeQuery(id+"F7dXQ7x4IlYUw1S_1.57.F3.boolean.opBoolean","MERGE",FACE,{"derivedFrom":[makeQuery(id+"F7dXQ7x4IlYUw1S_1.56.F3.boolean.opBoolean","MERGE",FACE,{"derivedFrom":[makeQuery(id+"F7dXQ7x4IlYUw1S_1.55.F3.boolean.opBoolean","MERGE",FACE,{"derivedFrom":[makeQuery(id+"F7dXQ7x4IlYUw1S_1.54.F3.boolean.opBoolean","MERGE",FACE,{"derivedFrom":[makeQuery(id+"F7dXQ7x4IlYUw1S_1.53.F3.boolean.opBoolean","MERGE",FACE,{"derivedFrom":[makeQuery(id+"F7dXQ7x4IlYUw1S_1.52.F3.boolean.opBoolean","MERGE",FACE,{"derivedFrom":[makeQuery(id+"F7dXQ7x4IlYUw1S_1.51.F3.boolean.opBoolean","MERGE",FACE,{"derivedFrom":[makeQuery(id+"F7dXQ7x4IlYUw1S_1.50.F3.boolean.opBoolean","MERGE",FACE,{"derivedFrom":[makeQuery(id+"F7dXQ7x4IlYUw1S_1.49.F3.boolean.opBoolean","MERGE",FACE,{"derivedFrom":[makeQuery(id+"F7dXQ7x4IlYUw1S_1.48.F3.boolean.opBoolean","MERGE",FACE,{"derivedFrom":[makeQuery(id+"F7dXQ7x4IlYUw1S_1.47.F3.boolean.opBoolean","MERGE",FACE,{"derivedFrom":[makeQuery(id+"F7dXQ7x4IlYUw1S_1.46.F3.boolean.opBoolean","MERGE",FACE,{"derivedFrom":[makeQuery(id+"F7dXQ7x4IlYUw1S_1.45.F3.boolean.opBoolean","MERGE",FACE,{"derivedFrom":[makeQuery(id+"F7dXQ7x4IlYUw1S_1.44.F3.boolean.opBoolean","MERGE",FACE,{"derivedFrom":[makeQuery(id+"F7dXQ7x4IlYUw1S_1.43.F3.boolean.opBoolean","MERGE",FACE,{"derivedFrom":[makeQuery(id+"F7dXQ7x4IlYUw1S_1.42.F3.boolean.opBoolean","MERGE",FACE,{"derivedFrom":[makeQuery(id+"F7dXQ7x4IlYUw1S_1.41.F3.boolean.opBoolean","MERGE",FACE,{"derivedFrom":[makeQuery(id+"F7dXQ7x4IlYUw1S_1.40.F3.boolean.opBoolean","MERGE",FACE,{"derivedFrom":[makeQuery(id+"F7dXQ7x4IlYUw1S_1.39.F3.boolean.opBoolean","MERGE",FACE,{"derivedFrom":[makeQuery(id+"F7dXQ7x4IlYUw1S_1.38.F3.boolean.opBoolean","MERGE",FACE,{"derivedFrom":[makeQuery(id+"F7dXQ7x4IlYUw1S_1.37.F3.boolean.opBoolean","MERGE",FACE,{"derivedFrom":[makeQuery(id+"F7dXQ7x4IlYUw1S_1.36.F3.boolean.opBoolean","MERGE",FACE,{"derivedFrom":[makeQuery(id+"F7dXQ7x4IlYUw1S_1.35.F3.boolean.opBoolean","MERGE",FACE,{"derivedFrom":[makeQuery(id+"F7dXQ7x4IlYUw1S_1.34.F3.boolean.opBoolean","MERGE",FACE,{"derivedFrom":[makeQuery(id+"F7dXQ7x4IlYUw1S_1.33.F3.boolean.opBoolean","MERGE",FACE,{"derivedFrom":[makeQuery(id+"F7dXQ7x4IlYUw1S_1.32.F3.boolean.opBoolean","MERGE",FACE,{"derivedFrom":[makeQuery(id+"F7dXQ7x4IlYUw1S_1.31.F3.boolean.opBoolean","MERGE",FACE,{"derivedFrom":[makeQuery(id+"F7dXQ7x4IlYUw1S_1.30.F3.boolean.opBoolean","MERGE",FACE,{"derivedFrom":[makeQuery(id+"F7dXQ7x4IlYUw1S_1.29.F3.boolean.opBoolean","MERGE",FACE,{"derivedFrom":[makeQuery(id+"F7dXQ7x4IlYUw1S_1.28.F3.boolean.opBoolean","MERGE",FACE,{"derivedFrom":[makeQuery(id+"F7dXQ7x4IlYUw1S_1.27.F3.boolean.opBoolean","MERGE",FACE,{"derivedFrom":[makeQuery(id+"F7dXQ7x4IlYUw1S_1.26.F3.boolean.opBoolean","MERGE",FACE,{"derivedFrom":[makeQuery(id+"F7dXQ7x4IlYUw1S_1.25.F3.boolean.opBoolean","MERGE",FACE,{"derivedFrom":[makeQuery(id+"F7dXQ7x4IlYUw1S_1.24.F3.boolean.opBoolean","MERGE",FACE,{"derivedFrom":[makeQuery(id+"F7dXQ7x4IlYUw1S_1.23.F3.boolean.opBoolean","MERGE",FACE,{"derivedFrom":[makeQuery(id+"F7dXQ7x4IlYUw1S_1.22.F3.boolean.opBoolean","MERGE",FACE,{"derivedFrom":[makeQuery(id+"F7dXQ7x4IlYUw1S_1.21.F3.boolean.opBoolean","MERGE",FACE,{"derivedFrom":[makeQuery(id+"F7dXQ7x4IlYUw1S_1.20.F3.boolean.opBoolean","MERGE",FACE,{"derivedFrom":[makeQuery(id+"F7dXQ7x4IlYUw1S_1.19.F3.boolean.opBoolean","MERGE",FACE,{"derivedFrom":[makeQuery(id+"F7dXQ7x4IlYUw1S_1.18.F3.boolean.opBoolean","MERGE",FACE,{"derivedFrom":[makeQuery(id+"F7dXQ7x4IlYUw1S_1.17.F3.boolean.opBoolean","MERGE",FACE,{"derivedFrom":[makeQuery(id+"F7dXQ7x4IlYUw1S_1.16.F3.boolean.opBoolean","MERGE",FACE,{"derivedFrom":[makeQuery(id+"F7dXQ7x4IlYUw1S_1.15.F3.boolean.opBoolean","MERGE",FACE,{"derivedFrom":[makeQuery(id+"F7dXQ7x4IlYUw1S_1.14.F3.boolean.opBoolean","MERGE",FACE,{"derivedFrom":[makeQuery(id+"F7dXQ7x4IlYUw1S_1.13.F3.boolean.opBoolean","MERGE",FACE,{"derivedFrom":[makeQuery(id+"F7dXQ7x4IlYUw1S_1.12.F3.boolean.opBoolean","MERGE",FACE,{"derivedFrom":[makeQuery(id+"F7dXQ7x4IlYUw1S_1.11.F3.boolean.opBoolean","MERGE",FACE,{"derivedFrom":[makeQuery(id+"F7dXQ7x4IlYUw1S_1.10.F3.boolean.opBoolean","MERGE",FACE,{"derivedFrom":[makeQuery(id+"F7dXQ7x4IlYUw1S_1.9.F3.boolean.opBoolean","MERGE",FACE,{"derivedFrom":[makeQuery(id+"F7dXQ7x4IlYUw1S_1.8.F3.boolean.opBoolean","MERGE",FACE,{"derivedFrom":[makeQuery(id+"F7dXQ7x4IlYUw1S_1.7.F3.boolean.opBoolean","MERGE",FACE,{"derivedFrom":[makeQuery(id+"F7dXQ7x4IlYUw1S_1.6.F3.boolean.opBoolean","MERGE",FACE,{"derivedFrom":[makeQuery(id+"F7dXQ7x4IlYUw1S_1.5.F3.boolean.opBoolean","MERGE",FACE,{"derivedFrom":[makeQuery(id+"F7dXQ7x4IlYUw1S_1.4.F3.boolean.opBoolean","MERGE",FACE,{"derivedFrom":[makeQuery(id+"F7dXQ7x4IlYUw1S_1.3.F3.boolean.opBoolean","MERGE",FACE,{"derivedFrom":[makeQuery(id+"F7dXQ7x4IlYUw1S_1.2.F3.boolean.opBoolean","MERGE",FACE,{"derivedFrom":[makeQuery(id+"F7dXQ7x4IlYUw1S_1.1.F3.boolean.opBoolean","MERGE",FACE,{"derivedFrom":[makeQuery(id+"F3.boolean.opBoolean","MERGE",FACE,{"derivedFrom":[makeQuery(id+"F1.opExtrude","CAP_FACE",FACE,{"disambiguationData":[OSD([sQuery(id+"F0.wireOp",EDGE,"E0")])],"isStart":false}),makeQuery(id+"F3.opExtrude","CAP_FACE",FACE,{"disambiguationData":[OSD([subQ3,subQ2,subQ1,subQ0])],"isStart":false})]}),makeQuery(id+"F7dXQ7x4IlYUw1S_1.1.F3.opExtrude","CAP_FACE",FACE,{"disambiguationData":[OSD([subQ3,subQ2,subQ1,subQ0])],"isStart":false})]}),makeQuery(id+"F7dXQ7x4IlYUw1S_1.2.F3.opExtrude","CAP_FACE",FACE,{"disambiguationData":[OSD([subQ3,subQ2,subQ1,subQ0])],"isStart":false})]}),makeQuery(id+"F7dXQ7x4IlYUw1S_1.3.F3.opExtrude","CAP_FACE",FACE,{"disambiguationData":[OSD([subQ3,subQ2,subQ1,subQ0])],"isStart":false})]}),makeQuery(id+"F7dXQ7x4IlYUw1S_1.4.F3.opExtrude","CAP_FACE",FACE,{"disambiguationData":[OSD([subQ3,subQ2,subQ1,subQ0])],"isStart":false})]}),makeQuery(id+"F7dXQ7x4IlYUw1S_1.5.F3.opExtrude","CAP_FACE",FACE,{"disambiguationData":[OSD([subQ3,subQ2,subQ1,subQ0])],"isStart":false})]}),makeQuery(id+"F7dXQ7x4IlYUw1S_1.6.F3.opExtrude","CAP_FACE",FACE,{"disambiguationData":[OSD([subQ3,subQ2,subQ1,subQ0])],"isStart":false})]}),makeQuery(id+"F7dXQ7x4IlYUw1S_1.7.F3.opExtrude","CAP_FACE",FACE,{"disambiguationData":[OSD([subQ3,subQ2,subQ1,subQ0])],"isStart":false})]}),makeQuery(id+"F7dXQ7x4IlYUw1S_1.8.F3.opExtrude","CAP_FACE",FACE,{"disambiguationData":[OSD([subQ3,subQ2,subQ1,subQ0])],"isStart":false})]}),makeQuery(id+"F7dXQ7x4IlYUw1S_1.9.F3.opExtrude","CAP_FACE",FACE,{"disambiguationData":[OSD([subQ3,subQ2,subQ1,subQ0])],"isStart":false})]}),makeQuery(id+"F7dXQ7x4IlYUw1S_1.10.F3.opExtrude","CAP_FACE",FACE,{"disambiguationData":[OSD([subQ3,subQ2,subQ1,subQ0])],"isStart":false})]}),makeQuery(id+"F7dXQ7x4IlYUw1S_1.11.F3.opExtrude","CAP_FACE",FACE,{"disambiguationData":[OSD([subQ3,subQ2,subQ1,subQ0])],"isStart":false})]}),makeQuery(id+"F7dXQ7x4IlYUw1S_1.12.F3.opExtrude","CAP_FACE",FACE,{"disambiguationData":[OSD([subQ3,subQ2,subQ1,subQ0])],"isStart":false})]}),makeQuery(id+"F7dXQ7x4IlYUw1S_1.13.F3.opExtrude","CAP_FACE",FACE,{"disambiguationData":[OSD([subQ3,subQ2,subQ1,subQ0])],"isStart":false})]}),makeQuery(id+"F7dXQ7x4IlYUw1S_1.14.F3.opExtrude","CAP_FACE",FACE,{"disambiguationData":[OSD([subQ3,subQ2,subQ1,subQ0])],"isStart":false})]}),makeQuery(id+"F7dXQ7x4IlYUw1S_1.15.F3.opExtrude","CAP_FACE",FACE,{"disambiguationData":[OSD([subQ3,subQ2,subQ1,subQ0])],"isStart":false})]}),makeQuery(id+"F7dXQ7x4IlYUw1S_1.16.F3.opExtrude","CAP_FACE",FACE,{"disambiguationData":[OSD([subQ3,subQ2,subQ1,subQ0])],"isStart":false})]}),makeQuery(id+"F7dXQ7x4IlYUw1S_1.17.F3.opExtrude","CAP_FACE",FACE,{"disambiguationData":[OSD([subQ3,subQ2,subQ1,subQ0])],"isStart":false})]}),makeQuery(id+"F7dXQ7x4IlYUw1S_1.18.F3.opExtrude","CAP_FACE",FACE,{"disambiguationData":[OSD([subQ3,subQ2,subQ1,subQ0])],"isStart":false})]}),makeQuery(id+"F7dXQ7x4IlYUw1S_1.19.F3.opExtrude","CAP_FACE",FACE,{"disambiguationData":[OSD([subQ3,subQ2,subQ1,subQ0])],"isStart":false})]}),makeQuery(id+"F7dXQ7x4IlYUw1S_1.20.F3.opExtrude","CAP_FACE",FACE,{"disambiguationData":[OSD([subQ3,subQ2,subQ1,subQ0])],"isStart":false})]}),makeQuery(id+"F7dXQ7x4IlYUw1S_1.21.F3.opExtrude","CAP_FACE",FACE,{"disambiguationData":[OSD([subQ3,subQ2,subQ1,subQ0])],"isStart":false})]}),makeQuery(id+"F7dXQ7x4IlYUw1S_1.22.F3.opExtrude","CAP_FACE",FACE,{"disambiguationData":[OSD([subQ3,subQ2,subQ1,subQ0])],"isStart":false})]}),makeQuery(id+"F7dXQ7x4IlYUw1S_1.23.F3.opExtrude","CAP_FACE",FACE,{"disambiguationData":[OSD([subQ3,subQ2,subQ1,subQ0])],"isStart":false})]}),makeQuery(id+"F7dXQ7x4IlYUw1S_1.24.F3.opExtrude","CAP_FACE",FACE,{"disambiguationData":[OSD([subQ3,subQ2,subQ1,subQ0])],"isStart":false})]}),makeQuery(id+"F7dXQ7x4IlYUw1S_1.25.F3.opExtrude","CAP_FACE",FACE,{"disambiguationData":[OSD([subQ3,subQ2,subQ1,subQ0])],"isStart":false})]}),makeQuery(id+"F7dXQ7x4IlYUw1S_1.26.F3.opExtrude","CAP_FACE",FACE,{"disambiguationData":[OSD([subQ3,subQ2,subQ1,subQ0])],"isStart":false})]}),makeQuery(id+"F7dXQ7x4IlYUw1S_1.27.F3.opExtrude","CAP_FACE",FACE,{"disambiguationData":[OSD([subQ3,subQ2,subQ1,subQ0])],"isStart":false})]}),makeQuery(id+"F7dXQ7x4IlYUw1S_1.28.F3.opExtrude","CAP_FACE",FACE,{"disambiguationData":[OSD([subQ3,subQ2,subQ1,subQ0])],"isStart":false})]}),makeQuery(id+"F7dXQ7x4IlYUw1S_1.29.F3.opExtrude","CAP_FACE",FACE,{"disambiguationData":[OSD([subQ3,subQ2,subQ1,subQ0])],"isStart":false})]}),makeQuery(id+"F7dXQ7x4IlYUw1S_1.30.F3.opExtrude","CAP_FACE",FACE,{"disambiguationData":[OSD([subQ3,subQ2,subQ1,subQ0])],"isStart":false})]}),makeQuery(id+"F7dXQ7x4IlYUw1S_1.31.F3.opExtrude","CAP_FACE",FACE,{"disambiguationData":[OSD([subQ3,subQ2,subQ1,subQ0])],"isStart":false})]}),makeQuery(id+"F7dXQ7x4IlYUw1S_1.32.F3.opExtrude","CAP_FACE",FACE,{"disambiguationData":[OSD([subQ3,subQ2,subQ1,subQ0])],"isStart":false})]}),makeQuery(id+"F7dXQ7x4IlYUw1S_1.33.F3.opExtrude","CAP_FACE",FACE,{"disambiguationData":[OSD([subQ3,subQ2,subQ1,subQ0])],"isStart":false})]}),makeQuery(id+"F7dXQ7x4IlYUw1S_1.34.F3.opExtrude","CAP_FACE",FACE,{"disambiguationData":[OSD([subQ3,subQ2,subQ1,subQ0])],"isStart":false})]}),makeQuery(id+"F7dXQ7x4IlYUw1S_1.35.F3.opExtrude","CAP_FACE",FACE,{"disambiguationData":[OSD([subQ3,subQ2,subQ1,subQ0])],"isStart":false})]}),makeQuery(id+"F7dXQ7x4IlYUw1S_1.36.F3.opExtrude","CAP_FACE",FACE,{"disambiguationData":[OSD([subQ3,subQ2,subQ1,subQ0])],"isStart":false})]}),makeQuery(id+"F7dXQ7x4IlYUw1S_1.37.F3.opExtrude","CAP_FACE",FACE,{"disambiguationData":[OSD([subQ3,subQ2,subQ1,subQ0])],"isStart":false})]}),makeQuery(id+"F7dXQ7x4IlYUw1S_1.38.F3.opExtrude","CAP_FACE",FACE,{"disambiguationData":[OSD([subQ3,subQ2,subQ1,subQ0])],"isStart":false})]}),makeQuery(id+"F7dXQ7x4IlYUw1S_1.39.F3.opExtrude","CAP_FACE",FACE,{"disambiguationData":[OSD([subQ3,subQ2,subQ1,subQ0])],"isStart":false})]}),makeQuery(id+"F7dXQ7x4IlYUw1S_1.40.F3.opExtrude","CAP_FACE",FACE,{"disambiguationData":[OSD([subQ3,subQ2,subQ1,subQ0])],"isStart":false})]}),makeQuery(id+"F7dXQ7x4IlYUw1S_1.41.F3.opExtrude","CAP_FACE",FACE,{"disambiguationData":[OSD([subQ3,subQ2,subQ1,subQ0])],"isStart":false})]}),makeQuery(id+"F7dXQ7x4IlYUw1S_1.42.F3.opExtrude","CAP_FACE",FACE,{"disambiguationData":[OSD([subQ3,subQ2,subQ1,subQ0])],"isStart":false})]}),makeQuery(id+"F7dXQ7x4IlYUw1S_1.43.F3.opExtrude","CAP_FACE",FACE,{"disambiguationData":[OSD([subQ3,subQ2,subQ1,subQ0])],"isStart":false})]}),makeQuery(id+"F7dXQ7x4IlYUw1S_1.44.F3.opExtrude","CAP_FACE",FACE,{"disambiguationData":[OSD([subQ3,subQ2,subQ1,subQ0])],"isStart":false})]}),makeQuery(id+"F7dXQ7x4IlYUw1S_1.45.F3.opExtrude","CAP_FACE",FACE,{"disambiguationData":[OSD([subQ3,subQ2,subQ1,subQ0])],"isStart":false})]}),makeQuery(id+"F7dXQ7x4IlYUw1S_1.46.F3.opExtrude","CAP_FACE",FACE,{"disambiguationData":[OSD([subQ3,subQ2,subQ1,subQ0])],"isStart":false})]}),makeQuery(id+"F7dXQ7x4IlYUw1S_1.47.F3.opExtrude","CAP_FACE",FACE,{"disambiguationData":[OSD([subQ3,subQ2,subQ1,subQ0])],"isStart":false})]}),makeQuery(id+"F7dXQ7x4IlYUw1S_1.48.F3.opExtrude","CAP_FACE",FACE,{"disambiguationData":[OSD([subQ3,subQ2,subQ1,subQ0])],"isStart":false})]}),makeQuery(id+"F7dXQ7x4IlYUw1S_1.49.F3.opExtrude","CAP_FACE",FACE,{"disambiguationData":[OSD([subQ3,subQ2,subQ1,subQ0])],"isStart":false})]}),makeQuery(id+"F7dXQ7x4IlYUw1S_1.50.F3.opExtrude","CAP_FACE",FACE,{"disambiguationData":[OSD([subQ3,subQ2,subQ1,subQ0])],"isStart":false})]}),makeQuery(id+"F7dXQ7x4IlYUw1S_1.51.F3.opExtrude","CAP_FACE",FACE,{"disambiguationData":[OSD([subQ3,subQ2,subQ1,subQ0])],"isStart":false})]}),makeQuery(id+"F7dXQ7x4IlYUw1S_1.52.F3.opExtrude","CAP_FACE",FACE,{"disambiguationData":[OSD([subQ3,subQ2,subQ1,subQ0])],"isStart":false})]}),makeQuery(id+"F7dXQ7x4IlYUw1S_1.53.F3.opExtrude","CAP_FACE",FACE,{"disambiguationData":[OSD([subQ3,subQ2,subQ1,subQ0])],"isStart":false})]}),makeQuery(id+"F7dXQ7x4IlYUw1S_1.54.F3.opExtrude","CAP_FACE",FACE,{"disambiguationData":[OSD([subQ3,subQ2,subQ1,subQ0])],"isStart":false})]}),makeQuery(id+"F7dXQ7x4IlYUw1S_1.55.F3.opExtrude","CAP_FACE",FACE,{"disambiguationData":[OSD([subQ3,subQ2,subQ1,subQ0])],"isStart":false})]}),makeQuery(id+"F7dXQ7x4IlYUw1S_1.56.F3.opExtrude","CAP_FACE",FACE,{"disambiguationData":[OSD([subQ3,subQ2,subQ1,subQ0])],"isStart":false})]}),makeQuery(id+"F7dXQ7x4IlYUw1S_1.57.F3.opExtrude","CAP_FACE",FACE,{"disambiguationData":[OSD([subQ3,subQ2,subQ1,subQ0])],"isStart":false})]}),makeQuery(id+"F7dXQ7x4IlYUw1S_1.58.F3.opExtrude","CAP_FACE",FACE,{"disambiguationData":[OSD([subQ3,subQ2,subQ1,subQ0])],"isStart":false})]}),makeQuery(id+"F7dXQ7x4IlYUw1S_1.59.F3.opExtrude","CAP_FACE",FACE,{"disambiguationData":[OSD([subQ3,subQ2,subQ1,subQ0])],"isStart":false})]});}
            cPlane(context, id + "F12", {"entities" : qUnion([Q0, Q1]), "cplaneType" : CPlaneType.MID_PLANE, "offset" : 25 * mm, "width" : 150 * mm, "height" : 150 * mm});
        }
        {
            var Q0;
            {var subQ0=sQuery(id+"F2.wireOp",EDGE,"E7");var subQ1=sQuery(id+"F2.wireOp",EDGE,"E6");var subQ2=sQuery(id+"F2.wireOp",EDGE,"E3");var subQ3=sQuery(id+"F2.wireOp",EDGE,"E2");Q0=makeQuery(id+"F7dXQ7x4IlYUw1S_1.59.F3.boolean.opBoolean","MERGE",FACE,{"derivedFrom":[makeQuery(id+"F7dXQ7x4IlYUw1S_1.58.F3.boolean.opBoolean","MERGE",FACE,{"derivedFrom":[makeQuery(id+"F7dXQ7x4IlYUw1S_1.57.F3.boolean.opBoolean","MERGE",FACE,{"derivedFrom":[makeQuery(id+"F7dXQ7x4IlYUw1S_1.56.F3.boolean.opBoolean","MERGE",FACE,{"derivedFrom":[makeQuery(id+"F7dXQ7x4IlYUw1S_1.55.F3.boolean.opBoolean","MERGE",FACE,{"derivedFrom":[makeQuery(id+"F7dXQ7x4IlYUw1S_1.54.F3.boolean.opBoolean","MERGE",FACE,{"derivedFrom":[makeQuery(id+"F7dXQ7x4IlYUw1S_1.53.F3.boolean.opBoolean","MERGE",FACE,{"derivedFrom":[makeQuery(id+"F7dXQ7x4IlYUw1S_1.52.F3.boolean.opBoolean","MERGE",FACE,{"derivedFrom":[makeQuery(id+"F7dXQ7x4IlYUw1S_1.51.F3.boolean.opBoolean","MERGE",FACE,{"derivedFrom":[makeQuery(id+"F7dXQ7x4IlYUw1S_1.50.F3.boolean.opBoolean","MERGE",FACE,{"derivedFrom":[makeQuery(id+"F7dXQ7x4IlYUw1S_1.49.F3.boolean.opBoolean","MERGE",FACE,{"derivedFrom":[makeQuery(id+"F7dXQ7x4IlYUw1S_1.48.F3.boolean.opBoolean","MERGE",FACE,{"derivedFrom":[makeQuery(id+"F7dXQ7x4IlYUw1S_1.47.F3.boolean.opBoolean","MERGE",FACE,{"derivedFrom":[makeQuery(id+"F7dXQ7x4IlYUw1S_1.46.F3.boolean.opBoolean","MERGE",FACE,{"derivedFrom":[makeQuery(id+"F7dXQ7x4IlYUw1S_1.45.F3.boolean.opBoolean","MERGE",FACE,{"derivedFrom":[makeQuery(id+"F7dXQ7x4IlYUw1S_1.44.F3.boolean.opBoolean","MERGE",FACE,{"derivedFrom":[makeQuery(id+"F7dXQ7x4IlYUw1S_1.43.F3.boolean.opBoolean","MERGE",FACE,{"derivedFrom":[makeQuery(id+"F7dXQ7x4IlYUw1S_1.42.F3.boolean.opBoolean","MERGE",FACE,{"derivedFrom":[makeQuery(id+"F7dXQ7x4IlYUw1S_1.41.F3.boolean.opBoolean","MERGE",FACE,{"derivedFrom":[makeQuery(id+"F7dXQ7x4IlYUw1S_1.40.F3.boolean.opBoolean","MERGE",FACE,{"derivedFrom":[makeQuery(id+"F7dXQ7x4IlYUw1S_1.39.F3.boolean.opBoolean","MERGE",FACE,{"derivedFrom":[makeQuery(id+"F7dXQ7x4IlYUw1S_1.38.F3.boolean.opBoolean","MERGE",FACE,{"derivedFrom":[makeQuery(id+"F7dXQ7x4IlYUw1S_1.37.F3.boolean.opBoolean","MERGE",FACE,{"derivedFrom":[makeQuery(id+"F7dXQ7x4IlYUw1S_1.36.F3.boolean.opBoolean","MERGE",FACE,{"derivedFrom":[makeQuery(id+"F7dXQ7x4IlYUw1S_1.35.F3.boolean.opBoolean","MERGE",FACE,{"derivedFrom":[makeQuery(id+"F7dXQ7x4IlYUw1S_1.34.F3.boolean.opBoolean","MERGE",FACE,{"derivedFrom":[makeQuery(id+"F7dXQ7x4IlYUw1S_1.33.F3.boolean.opBoolean","MERGE",FACE,{"derivedFrom":[makeQuery(id+"F7dXQ7x4IlYUw1S_1.32.F3.boolean.opBoolean","MERGE",FACE,{"derivedFrom":[makeQuery(id+"F7dXQ7x4IlYUw1S_1.31.F3.boolean.opBoolean","MERGE",FACE,{"derivedFrom":[makeQuery(id+"F7dXQ7x4IlYUw1S_1.30.F3.boolean.opBoolean","MERGE",FACE,{"derivedFrom":[makeQuery(id+"F7dXQ7x4IlYUw1S_1.29.F3.boolean.opBoolean","MERGE",FACE,{"derivedFrom":[makeQuery(id+"F7dXQ7x4IlYUw1S_1.28.F3.boolean.opBoolean","MERGE",FACE,{"derivedFrom":[makeQuery(id+"F7dXQ7x4IlYUw1S_1.27.F3.boolean.opBoolean","MERGE",FACE,{"derivedFrom":[makeQuery(id+"F7dXQ7x4IlYUw1S_1.26.F3.boolean.opBoolean","MERGE",FACE,{"derivedFrom":[makeQuery(id+"F7dXQ7x4IlYUw1S_1.25.F3.boolean.opBoolean","MERGE",FACE,{"derivedFrom":[makeQuery(id+"F7dXQ7x4IlYUw1S_1.24.F3.boolean.opBoolean","MERGE",FACE,{"derivedFrom":[makeQuery(id+"F7dXQ7x4IlYUw1S_1.23.F3.boolean.opBoolean","MERGE",FACE,{"derivedFrom":[makeQuery(id+"F7dXQ7x4IlYUw1S_1.22.F3.boolean.opBoolean","MERGE",FACE,{"derivedFrom":[makeQuery(id+"F7dXQ7x4IlYUw1S_1.21.F3.boolean.opBoolean","MERGE",FACE,{"derivedFrom":[makeQuery(id+"F7dXQ7x4IlYUw1S_1.20.F3.boolean.opBoolean","MERGE",FACE,{"derivedFrom":[makeQuery(id+"F7dXQ7x4IlYUw1S_1.19.F3.boolean.opBoolean","MERGE",FACE,{"derivedFrom":[makeQuery(id+"F7dXQ7x4IlYUw1S_1.18.F3.boolean.opBoolean","MERGE",FACE,{"derivedFrom":[makeQuery(id+"F7dXQ7x4IlYUw1S_1.17.F3.boolean.opBoolean","MERGE",FACE,{"derivedFrom":[makeQuery(id+"F7dXQ7x4IlYUw1S_1.16.F3.boolean.opBoolean","MERGE",FACE,{"derivedFrom":[makeQuery(id+"F7dXQ7x4IlYUw1S_1.15.F3.boolean.opBoolean","MERGE",FACE,{"derivedFrom":[makeQuery(id+"F7dXQ7x4IlYUw1S_1.14.F3.boolean.opBoolean","MERGE",FACE,{"derivedFrom":[makeQuery(id+"F7dXQ7x4IlYUw1S_1.13.F3.boolean.opBoolean","MERGE",FACE,{"derivedFrom":[makeQuery(id+"F7dXQ7x4IlYUw1S_1.12.F3.boolean.opBoolean","MERGE",FACE,{"derivedFrom":[makeQuery(id+"F7dXQ7x4IlYUw1S_1.11.F3.boolean.opBoolean","MERGE",FACE,{"derivedFrom":[makeQuery(id+"F7dXQ7x4IlYUw1S_1.10.F3.boolean.opBoolean","MERGE",FACE,{"derivedFrom":[makeQuery(id+"F7dXQ7x4IlYUw1S_1.9.F3.boolean.opBoolean","MERGE",FACE,{"derivedFrom":[makeQuery(id+"F7dXQ7x4IlYUw1S_1.8.F3.boolean.opBoolean","MERGE",FACE,{"derivedFrom":[makeQuery(id+"F7dXQ7x4IlYUw1S_1.7.F3.boolean.opBoolean","MERGE",FACE,{"derivedFrom":[makeQuery(id+"F7dXQ7x4IlYUw1S_1.6.F3.boolean.opBoolean","MERGE",FACE,{"derivedFrom":[makeQuery(id+"F7dXQ7x4IlYUw1S_1.5.F3.boolean.opBoolean","MERGE",FACE,{"derivedFrom":[makeQuery(id+"F7dXQ7x4IlYUw1S_1.4.F3.boolean.opBoolean","MERGE",FACE,{"derivedFrom":[makeQuery(id+"F7dXQ7x4IlYUw1S_1.3.F3.boolean.opBoolean","MERGE",FACE,{"derivedFrom":[makeQuery(id+"F7dXQ7x4IlYUw1S_1.2.F3.boolean.opBoolean","MERGE",FACE,{"derivedFrom":[makeQuery(id+"F7dXQ7x4IlYUw1S_1.1.F3.boolean.opBoolean","MERGE",FACE,{"derivedFrom":[makeQuery(id+"F3.boolean.opBoolean","MERGE",FACE,{"derivedFrom":[makeQuery(id+"F1.opExtrude","CAP_FACE",FACE,{"disambiguationData":[OSD([sQuery(id+"F0.wireOp",EDGE,"E0")])],"isStart":false}),makeQuery(id+"F3.opExtrude","CAP_FACE",FACE,{"disambiguationData":[OSD([subQ3,subQ2,subQ1,subQ0])],"isStart":false})]}),makeQuery(id+"F7dXQ7x4IlYUw1S_1.1.F3.opExtrude","CAP_FACE",FACE,{"disambiguationData":[OSD([subQ3,subQ2,subQ1,subQ0])],"isStart":false})]}),makeQuery(id+"F7dXQ7x4IlYUw1S_1.2.F3.opExtrude","CAP_FACE",FACE,{"disambiguationData":[OSD([subQ3,subQ2,subQ1,subQ0])],"isStart":false})]}),makeQuery(id+"F7dXQ7x4IlYUw1S_1.3.F3.opExtrude","CAP_FACE",FACE,{"disambiguationData":[OSD([subQ3,subQ2,subQ1,subQ0])],"isStart":false})]}),makeQuery(id+"F7dXQ7x4IlYUw1S_1.4.F3.opExtrude","CAP_FACE",FACE,{"disambiguationData":[OSD([subQ3,subQ2,subQ1,subQ0])],"isStart":false})]}),makeQuery(id+"F7dXQ7x4IlYUw1S_1.5.F3.opExtrude","CAP_FACE",FACE,{"disambiguationData":[OSD([subQ3,subQ2,subQ1,subQ0])],"isStart":false})]}),makeQuery(id+"F7dXQ7x4IlYUw1S_1.6.F3.opExtrude","CAP_FACE",FACE,{"disambiguationData":[OSD([subQ3,subQ2,subQ1,subQ0])],"isStart":false})]}),makeQuery(id+"F7dXQ7x4IlYUw1S_1.7.F3.opExtrude","CAP_FACE",FACE,{"disambiguationData":[OSD([subQ3,subQ2,subQ1,subQ0])],"isStart":false})]}),makeQuery(id+"F7dXQ7x4IlYUw1S_1.8.F3.opExtrude","CAP_FACE",FACE,{"disambiguationData":[OSD([subQ3,subQ2,subQ1,subQ0])],"isStart":false})]}),makeQuery(id+"F7dXQ7x4IlYUw1S_1.9.F3.opExtrude","CAP_FACE",FACE,{"disambiguationData":[OSD([subQ3,subQ2,subQ1,subQ0])],"isStart":false})]}),makeQuery(id+"F7dXQ7x4IlYUw1S_1.10.F3.opExtrude","CAP_FACE",FACE,{"disambiguationData":[OSD([subQ3,subQ2,subQ1,subQ0])],"isStart":false})]}),makeQuery(id+"F7dXQ7x4IlYUw1S_1.11.F3.opExtrude","CAP_FACE",FACE,{"disambiguationData":[OSD([subQ3,subQ2,subQ1,subQ0])],"isStart":false})]}),makeQuery(id+"F7dXQ7x4IlYUw1S_1.12.F3.opExtrude","CAP_FACE",FACE,{"disambiguationData":[OSD([subQ3,subQ2,subQ1,subQ0])],"isStart":false})]}),makeQuery(id+"F7dXQ7x4IlYUw1S_1.13.F3.opExtrude","CAP_FACE",FACE,{"disambiguationData":[OSD([subQ3,subQ2,subQ1,subQ0])],"isStart":false})]}),makeQuery(id+"F7dXQ7x4IlYUw1S_1.14.F3.opExtrude","CAP_FACE",FACE,{"disambiguationData":[OSD([subQ3,subQ2,subQ1,subQ0])],"isStart":false})]}),makeQuery(id+"F7dXQ7x4IlYUw1S_1.15.F3.opExtrude","CAP_FACE",FACE,{"disambiguationData":[OSD([subQ3,subQ2,subQ1,subQ0])],"isStart":false})]}),makeQuery(id+"F7dXQ7x4IlYUw1S_1.16.F3.opExtrude","CAP_FACE",FACE,{"disambiguationData":[OSD([subQ3,subQ2,subQ1,subQ0])],"isStart":false})]}),makeQuery(id+"F7dXQ7x4IlYUw1S_1.17.F3.opExtrude","CAP_FACE",FACE,{"disambiguationData":[OSD([subQ3,subQ2,subQ1,subQ0])],"isStart":false})]}),makeQuery(id+"F7dXQ7x4IlYUw1S_1.18.F3.opExtrude","CAP_FACE",FACE,{"disambiguationData":[OSD([subQ3,subQ2,subQ1,subQ0])],"isStart":false})]}),makeQuery(id+"F7dXQ7x4IlYUw1S_1.19.F3.opExtrude","CAP_FACE",FACE,{"disambiguationData":[OSD([subQ3,subQ2,subQ1,subQ0])],"isStart":false})]}),makeQuery(id+"F7dXQ7x4IlYUw1S_1.20.F3.opExtrude","CAP_FACE",FACE,{"disambiguationData":[OSD([subQ3,subQ2,subQ1,subQ0])],"isStart":false})]}),makeQuery(id+"F7dXQ7x4IlYUw1S_1.21.F3.opExtrude","CAP_FACE",FACE,{"disambiguationData":[OSD([subQ3,subQ2,subQ1,subQ0])],"isStart":false})]}),makeQuery(id+"F7dXQ7x4IlYUw1S_1.22.F3.opExtrude","CAP_FACE",FACE,{"disambiguationData":[OSD([subQ3,subQ2,subQ1,subQ0])],"isStart":false})]}),makeQuery(id+"F7dXQ7x4IlYUw1S_1.23.F3.opExtrude","CAP_FACE",FACE,{"disambiguationData":[OSD([subQ3,subQ2,subQ1,subQ0])],"isStart":false})]}),makeQuery(id+"F7dXQ7x4IlYUw1S_1.24.F3.opExtrude","CAP_FACE",FACE,{"disambiguationData":[OSD([subQ3,subQ2,subQ1,subQ0])],"isStart":false})]}),makeQuery(id+"F7dXQ7x4IlYUw1S_1.25.F3.opExtrude","CAP_FACE",FACE,{"disambiguationData":[OSD([subQ3,subQ2,subQ1,subQ0])],"isStart":false})]}),makeQuery(id+"F7dXQ7x4IlYUw1S_1.26.F3.opExtrude","CAP_FACE",FACE,{"disambiguationData":[OSD([subQ3,subQ2,subQ1,subQ0])],"isStart":false})]}),makeQuery(id+"F7dXQ7x4IlYUw1S_1.27.F3.opExtrude","CAP_FACE",FACE,{"disambiguationData":[OSD([subQ3,subQ2,subQ1,subQ0])],"isStart":false})]}),makeQuery(id+"F7dXQ7x4IlYUw1S_1.28.F3.opExtrude","CAP_FACE",FACE,{"disambiguationData":[OSD([subQ3,subQ2,subQ1,subQ0])],"isStart":false})]}),makeQuery(id+"F7dXQ7x4IlYUw1S_1.29.F3.opExtrude","CAP_FACE",FACE,{"disambiguationData":[OSD([subQ3,subQ2,subQ1,subQ0])],"isStart":false})]}),makeQuery(id+"F7dXQ7x4IlYUw1S_1.30.F3.opExtrude","CAP_FACE",FACE,{"disambiguationData":[OSD([subQ3,subQ2,subQ1,subQ0])],"isStart":false})]}),makeQuery(id+"F7dXQ7x4IlYUw1S_1.31.F3.opExtrude","CAP_FACE",FACE,{"disambiguationData":[OSD([subQ3,subQ2,subQ1,subQ0])],"isStart":false})]}),makeQuery(id+"F7dXQ7x4IlYUw1S_1.32.F3.opExtrude","CAP_FACE",FACE,{"disambiguationData":[OSD([subQ3,subQ2,subQ1,subQ0])],"isStart":false})]}),makeQuery(id+"F7dXQ7x4IlYUw1S_1.33.F3.opExtrude","CAP_FACE",FACE,{"disambiguationData":[OSD([subQ3,subQ2,subQ1,subQ0])],"isStart":false})]}),makeQuery(id+"F7dXQ7x4IlYUw1S_1.34.F3.opExtrude","CAP_FACE",FACE,{"disambiguationData":[OSD([subQ3,subQ2,subQ1,subQ0])],"isStart":false})]}),makeQuery(id+"F7dXQ7x4IlYUw1S_1.35.F3.opExtrude","CAP_FACE",FACE,{"disambiguationData":[OSD([subQ3,subQ2,subQ1,subQ0])],"isStart":false})]}),makeQuery(id+"F7dXQ7x4IlYUw1S_1.36.F3.opExtrude","CAP_FACE",FACE,{"disambiguationData":[OSD([subQ3,subQ2,subQ1,subQ0])],"isStart":false})]}),makeQuery(id+"F7dXQ7x4IlYUw1S_1.37.F3.opExtrude","CAP_FACE",FACE,{"disambiguationData":[OSD([subQ3,subQ2,subQ1,subQ0])],"isStart":false})]}),makeQuery(id+"F7dXQ7x4IlYUw1S_1.38.F3.opExtrude","CAP_FACE",FACE,{"disambiguationData":[OSD([subQ3,subQ2,subQ1,subQ0])],"isStart":false})]}),makeQuery(id+"F7dXQ7x4IlYUw1S_1.39.F3.opExtrude","CAP_FACE",FACE,{"disambiguationData":[OSD([subQ3,subQ2,subQ1,subQ0])],"isStart":false})]}),makeQuery(id+"F7dXQ7x4IlYUw1S_1.40.F3.opExtrude","CAP_FACE",FACE,{"disambiguationData":[OSD([subQ3,subQ2,subQ1,subQ0])],"isStart":false})]}),makeQuery(id+"F7dXQ7x4IlYUw1S_1.41.F3.opExtrude","CAP_FACE",FACE,{"disambiguationData":[OSD([subQ3,subQ2,subQ1,subQ0])],"isStart":false})]}),makeQuery(id+"F7dXQ7x4IlYUw1S_1.42.F3.opExtrude","CAP_FACE",FACE,{"disambiguationData":[OSD([subQ3,subQ2,subQ1,subQ0])],"isStart":false})]}),makeQuery(id+"F7dXQ7x4IlYUw1S_1.43.F3.opExtrude","CAP_FACE",FACE,{"disambiguationData":[OSD([subQ3,subQ2,subQ1,subQ0])],"isStart":false})]}),makeQuery(id+"F7dXQ7x4IlYUw1S_1.44.F3.opExtrude","CAP_FACE",FACE,{"disambiguationData":[OSD([subQ3,subQ2,subQ1,subQ0])],"isStart":false})]}),makeQuery(id+"F7dXQ7x4IlYUw1S_1.45.F3.opExtrude","CAP_FACE",FACE,{"disambiguationData":[OSD([subQ3,subQ2,subQ1,subQ0])],"isStart":false})]}),makeQuery(id+"F7dXQ7x4IlYUw1S_1.46.F3.opExtrude","CAP_FACE",FACE,{"disambiguationData":[OSD([subQ3,subQ2,subQ1,subQ0])],"isStart":false})]}),makeQuery(id+"F7dXQ7x4IlYUw1S_1.47.F3.opExtrude","CAP_FACE",FACE,{"disambiguationData":[OSD([subQ3,subQ2,subQ1,subQ0])],"isStart":false})]}),makeQuery(id+"F7dXQ7x4IlYUw1S_1.48.F3.opExtrude","CAP_FACE",FACE,{"disambiguationData":[OSD([subQ3,subQ2,subQ1,subQ0])],"isStart":false})]}),makeQuery(id+"F7dXQ7x4IlYUw1S_1.49.F3.opExtrude","CAP_FACE",FACE,{"disambiguationData":[OSD([subQ3,subQ2,subQ1,subQ0])],"isStart":false})]}),makeQuery(id+"F7dXQ7x4IlYUw1S_1.50.F3.opExtrude","CAP_FACE",FACE,{"disambiguationData":[OSD([subQ3,subQ2,subQ1,subQ0])],"isStart":false})]}),makeQuery(id+"F7dXQ7x4IlYUw1S_1.51.F3.opExtrude","CAP_FACE",FACE,{"disambiguationData":[OSD([subQ3,subQ2,subQ1,subQ0])],"isStart":false})]}),makeQuery(id+"F7dXQ7x4IlYUw1S_1.52.F3.opExtrude","CAP_FACE",FACE,{"disambiguationData":[OSD([subQ3,subQ2,subQ1,subQ0])],"isStart":false})]}),makeQuery(id+"F7dXQ7x4IlYUw1S_1.53.F3.opExtrude","CAP_FACE",FACE,{"disambiguationData":[OSD([subQ3,subQ2,subQ1,subQ0])],"isStart":false})]}),makeQuery(id+"F7dXQ7x4IlYUw1S_1.54.F3.opExtrude","CAP_FACE",FACE,{"disambiguationData":[OSD([subQ3,subQ2,subQ1,subQ0])],"isStart":false})]}),makeQuery(id+"F7dXQ7x4IlYUw1S_1.55.F3.opExtrude","CAP_FACE",FACE,{"disambiguationData":[OSD([subQ3,subQ2,subQ1,subQ0])],"isStart":false})]}),makeQuery(id+"F7dXQ7x4IlYUw1S_1.56.F3.opExtrude","CAP_FACE",FACE,{"disambiguationData":[OSD([subQ3,subQ2,subQ1,subQ0])],"isStart":false})]}),makeQuery(id+"F7dXQ7x4IlYUw1S_1.57.F3.opExtrude","CAP_FACE",FACE,{"disambiguationData":[OSD([subQ3,subQ2,subQ1,subQ0])],"isStart":false})]}),makeQuery(id+"F7dXQ7x4IlYUw1S_1.58.F3.opExtrude","CAP_FACE",FACE,{"disambiguationData":[OSD([subQ3,subQ2,subQ1,subQ0])],"isStart":false})]}),makeQuery(id+"F7dXQ7x4IlYUw1S_1.59.F3.opExtrude","CAP_FACE",FACE,{"disambiguationData":[OSD([subQ3,subQ2,subQ1,subQ0])],"isStart":false})]});}
            var sketch = newSketch(context, id + "F13", { "sketchPlane" : qUnion([Q0])});
            skCircle(sketch, "E58", {"center": v(0, 0) * mm, "radius": 580 * mm});
            skSolve(sketch);
        }
        {
            var Q0;
            Q0=qSketchRegion(id+"F13",true);
            extrude(context, id + "F14", {"entities" : qUnion([Q0]), "operationType" : NewBodyOperationType.ADD, "depth" : 100 * mm});
        }
        {
            var Q0;
            Q0=makeQuery(id+"F5.opExtrude","CAP_EDGE",EDGE,{"disambiguationData":[OSD([sQuery(id+"F4.wireOp",EDGE,"E8")])],"isStart":false});
            chamfer(context, id + "F15", {"entities" : qUnion([Q0]), "width" : 20 * mm, "tangentPropagation" : true});
        }
        {
            var Q0;
            {var subQ0=sQuery(id+"F2.wireOp",EDGE,"E6");var subQ1=sQuery(id+"F2.wireOp",EDGE,"E3");var subQ2=sQuery(id+"F2.wireOp",EDGE,"E2");var subQ3=sQuery(id+"F0.wireOp",EDGE,"E0");var subQ4=sQuery(id+"F2.wireOp",EDGE,"E7");Q0=makeQuery(id+"F5.boolean.opBoolean","SPLIT",FACE,{"disambiguationData":[TD([makeQuery(id+"F7dXQ7x4IlYUw1S_1.11.F3.opExtrude","SWEPT_FACE",FACE,{"disambiguationData":[OSD([subQ2])]})])],"derivedFrom":makeQuery(id+"F7dXQ7x4IlYUw1S_1.59.F3.boolean.opBoolean","MERGE",FACE,{"derivedFrom":[makeQuery(id+"F7dXQ7x4IlYUw1S_1.58.F3.boolean.opBoolean","MERGE",FACE,{"derivedFrom":[makeQuery(id+"F7dXQ7x4IlYUw1S_1.57.F3.boolean.opBoolean","MERGE",FACE,{"derivedFrom":[makeQuery(id+"F7dXQ7x4IlYUw1S_1.56.F3.boolean.opBoolean","MERGE",FACE,{"derivedFrom":[makeQuery(id+"F7dXQ7x4IlYUw1S_1.55.F3.boolean.opBoolean","MERGE",FACE,{"derivedFrom":[makeQuery(id+"F7dXQ7x4IlYUw1S_1.54.F3.boolean.opBoolean","MERGE",FACE,{"derivedFrom":[makeQuery(id+"F7dXQ7x4IlYUw1S_1.53.F3.boolean.opBoolean","MERGE",FACE,{"derivedFrom":[makeQuery(id+"F7dXQ7x4IlYUw1S_1.52.F3.boolean.opBoolean","MERGE",FACE,{"derivedFrom":[makeQuery(id+"F7dXQ7x4IlYUw1S_1.51.F3.boolean.opBoolean","MERGE",FACE,{"derivedFrom":[makeQuery(id+"F7dXQ7x4IlYUw1S_1.50.F3.boolean.opBoolean","MERGE",FACE,{"derivedFrom":[makeQuery(id+"F7dXQ7x4IlYUw1S_1.49.F3.boolean.opBoolean","MERGE",FACE,{"derivedFrom":[makeQuery(id+"F7dXQ7x4IlYUw1S_1.48.F3.boolean.opBoolean","MERGE",FACE,{"derivedFrom":[makeQuery(id+"F7dXQ7x4IlYUw1S_1.47.F3.boolean.opBoolean","MERGE",FACE,{"derivedFrom":[makeQuery(id+"F7dXQ7x4IlYUw1S_1.46.F3.boolean.opBoolean","MERGE",FACE,{"derivedFrom":[makeQuery(id+"F7dXQ7x4IlYUw1S_1.45.F3.boolean.opBoolean","MERGE",FACE,{"derivedFrom":[makeQuery(id+"F7dXQ7x4IlYUw1S_1.44.F3.boolean.opBoolean","MERGE",FACE,{"derivedFrom":[makeQuery(id+"F7dXQ7x4IlYUw1S_1.43.F3.boolean.opBoolean","MERGE",FACE,{"derivedFrom":[makeQuery(id+"F7dXQ7x4IlYUw1S_1.42.F3.boolean.opBoolean","MERGE",FACE,{"derivedFrom":[makeQuery(id+"F7dXQ7x4IlYUw1S_1.41.F3.boolean.opBoolean","MERGE",FACE,{"derivedFrom":[makeQuery(id+"F7dXQ7x4IlYUw1S_1.40.F3.boolean.opBoolean","MERGE",FACE,{"derivedFrom":[makeQuery(id+"F7dXQ7x4IlYUw1S_1.39.F3.boolean.opBoolean","MERGE",FACE,{"derivedFrom":[makeQuery(id+"F7dXQ7x4IlYUw1S_1.38.F3.boolean.opBoolean","MERGE",FACE,{"derivedFrom":[makeQuery(id+"F7dXQ7x4IlYUw1S_1.37.F3.boolean.opBoolean","MERGE",FACE,{"derivedFrom":[makeQuery(id+"F7dXQ7x4IlYUw1S_1.36.F3.boolean.opBoolean","MERGE",FACE,{"derivedFrom":[makeQuery(id+"F7dXQ7x4IlYUw1S_1.35.F3.boolean.opBoolean","MERGE",FACE,{"derivedFrom":[makeQuery(id+"F7dXQ7x4IlYUw1S_1.34.F3.boolean.opBoolean","MERGE",FACE,{"derivedFrom":[makeQuery(id+"F7dXQ7x4IlYUw1S_1.33.F3.boolean.opBoolean","MERGE",FACE,{"derivedFrom":[makeQuery(id+"F7dXQ7x4IlYUw1S_1.32.F3.boolean.opBoolean","MERGE",FACE,{"derivedFrom":[makeQuery(id+"F7dXQ7x4IlYUw1S_1.31.F3.boolean.opBoolean","MERGE",FACE,{"derivedFrom":[makeQuery(id+"F7dXQ7x4IlYUw1S_1.30.F3.boolean.opBoolean","MERGE",FACE,{"derivedFrom":[makeQuery(id+"F7dXQ7x4IlYUw1S_1.29.F3.boolean.opBoolean","MERGE",FACE,{"derivedFrom":[makeQuery(id+"F7dXQ7x4IlYUw1S_1.28.F3.boolean.opBoolean","MERGE",FACE,{"derivedFrom":[makeQuery(id+"F7dXQ7x4IlYUw1S_1.27.F3.boolean.opBoolean","MERGE",FACE,{"derivedFrom":[makeQuery(id+"F7dXQ7x4IlYUw1S_1.26.F3.boolean.opBoolean","MERGE",FACE,{"derivedFrom":[makeQuery(id+"F7dXQ7x4IlYUw1S_1.25.F3.boolean.opBoolean","MERGE",FACE,{"derivedFrom":[makeQuery(id+"F7dXQ7x4IlYUw1S_1.24.F3.boolean.opBoolean","MERGE",FACE,{"derivedFrom":[makeQuery(id+"F7dXQ7x4IlYUw1S_1.23.F3.boolean.opBoolean","MERGE",FACE,{"derivedFrom":[makeQuery(id+"F7dXQ7x4IlYUw1S_1.22.F3.boolean.opBoolean","MERGE",FACE,{"derivedFrom":[makeQuery(id+"F7dXQ7x4IlYUw1S_1.21.F3.boolean.opBoolean","MERGE",FACE,{"derivedFrom":[makeQuery(id+"F7dXQ7x4IlYUw1S_1.20.F3.boolean.opBoolean","MERGE",FACE,{"derivedFrom":[makeQuery(id+"F7dXQ7x4IlYUw1S_1.19.F3.boolean.opBoolean","MERGE",FACE,{"derivedFrom":[makeQuery(id+"F7dXQ7x4IlYUw1S_1.18.F3.boolean.opBoolean","MERGE",FACE,{"derivedFrom":[makeQuery(id+"F7dXQ7x4IlYUw1S_1.17.F3.boolean.opBoolean","MERGE",FACE,{"derivedFrom":[makeQuery(id+"F7dXQ7x4IlYUw1S_1.16.F3.boolean.opBoolean","MERGE",FACE,{"derivedFrom":[makeQuery(id+"F7dXQ7x4IlYUw1S_1.15.F3.boolean.opBoolean","MERGE",FACE,{"derivedFrom":[makeQuery(id+"F7dXQ7x4IlYUw1S_1.14.F3.boolean.opBoolean","MERGE",FACE,{"derivedFrom":[makeQuery(id+"F7dXQ7x4IlYUw1S_1.13.F3.boolean.opBoolean","MERGE",FACE,{"derivedFrom":[makeQuery(id+"F7dXQ7x4IlYUw1S_1.12.F3.boolean.opBoolean","MERGE",FACE,{"derivedFrom":[makeQuery(id+"F7dXQ7x4IlYUw1S_1.11.F3.boolean.opBoolean","MERGE",FACE,{"derivedFrom":[makeQuery(id+"F7dXQ7x4IlYUw1S_1.10.F3.boolean.opBoolean","MERGE",FACE,{"derivedFrom":[makeQuery(id+"F7dXQ7x4IlYUw1S_1.9.F3.boolean.opBoolean","MERGE",FACE,{"derivedFrom":[makeQuery(id+"F7dXQ7x4IlYUw1S_1.8.F3.boolean.opBoolean","MERGE",FACE,{"derivedFrom":[makeQuery(id+"F7dXQ7x4IlYUw1S_1.7.F3.boolean.opBoolean","MERGE",FACE,{"derivedFrom":[makeQuery(id+"F7dXQ7x4IlYUw1S_1.6.F3.boolean.opBoolean","MERGE",FACE,{"derivedFrom":[makeQuery(id+"F7dXQ7x4IlYUw1S_1.5.F3.boolean.opBoolean","MERGE",FACE,{"derivedFrom":[makeQuery(id+"F7dXQ7x4IlYUw1S_1.4.F3.boolean.opBoolean","MERGE",FACE,{"derivedFrom":[makeQuery(id+"F7dXQ7x4IlYUw1S_1.3.F3.boolean.opBoolean","MERGE",FACE,{"derivedFrom":[makeQuery(id+"F7dXQ7x4IlYUw1S_1.2.F3.boolean.opBoolean","MERGE",FACE,{"derivedFrom":[makeQuery(id+"F7dXQ7x4IlYUw1S_1.1.F3.boolean.opBoolean","MERGE",FACE,{"derivedFrom":[makeQuery(id+"F3.boolean.opBoolean","MERGE",FACE,{"derivedFrom":[makeQuery(id+"F1.opExtrude","CAP_FACE",FACE,{"disambiguationData":[OSD([subQ3])],"isStart":true}),makeQuery(id+"F3.opExtrude","CAP_FACE",FACE,{"disambiguationData":[OSD([subQ2,subQ1,subQ0,subQ4])],"isStart":true})]}),makeQuery(id+"F7dXQ7x4IlYUw1S_1.1.F3.opExtrude","CAP_FACE",FACE,{"disambiguationData":[OSD([subQ2,subQ1,subQ0,subQ4])],"isStart":true})]}),makeQuery(id+"F7dXQ7x4IlYUw1S_1.2.F3.opExtrude","CAP_FACE",FACE,{"disambiguationData":[OSD([subQ2,subQ1,subQ0,subQ4])],"isStart":true})]}),makeQuery(id+"F7dXQ7x4IlYUw1S_1.3.F3.opExtrude","CAP_FACE",FACE,{"disambiguationData":[OSD([subQ2,subQ1,subQ0,subQ4])],"isStart":true})]}),makeQuery(id+"F7dXQ7x4IlYUw1S_1.4.F3.opExtrude","CAP_FACE",FACE,{"disambiguationData":[OSD([subQ2,subQ1,subQ0,subQ4])],"isStart":true})]}),makeQuery(id+"F7dXQ7x4IlYUw1S_1.5.F3.opExtrude","CAP_FACE",FACE,{"disambiguationData":[OSD([subQ2,subQ1,subQ0,subQ4])],"isStart":true})]}),makeQuery(id+"F7dXQ7x4IlYUw1S_1.6.F3.opExtrude","CAP_FACE",FACE,{"disambiguationData":[OSD([subQ2,subQ1,subQ0,subQ4])],"isStart":true})]}),makeQuery(id+"F7dXQ7x4IlYUw1S_1.7.F3.opExtrude","CAP_FACE",FACE,{"disambiguationData":[OSD([subQ2,subQ1,subQ0,subQ4])],"isStart":true})]}),makeQuery(id+"F7dXQ7x4IlYUw1S_1.8.F3.opExtrude","CAP_FACE",FACE,{"disambiguationData":[OSD([subQ2,subQ1,subQ0,subQ4])],"isStart":true})]}),makeQuery(id+"F7dXQ7x4IlYUw1S_1.9.F3.opExtrude","CAP_FACE",FACE,{"disambiguationData":[OSD([subQ2,subQ1,subQ0,subQ4])],"isStart":true})]}),makeQuery(id+"F7dXQ7x4IlYUw1S_1.10.F3.opExtrude","CAP_FACE",FACE,{"disambiguationData":[OSD([subQ2,subQ1,subQ0,subQ4])],"isStart":true})]}),makeQuery(id+"F7dXQ7x4IlYUw1S_1.11.F3.opExtrude","CAP_FACE",FACE,{"disambiguationData":[OSD([subQ2,subQ1,subQ0,subQ4])],"isStart":true})]}),makeQuery(id+"F7dXQ7x4IlYUw1S_1.12.F3.opExtrude","CAP_FACE",FACE,{"disambiguationData":[OSD([subQ2,subQ1,subQ0,subQ4])],"isStart":true})]}),makeQuery(id+"F7dXQ7x4IlYUw1S_1.13.F3.opExtrude","CAP_FACE",FACE,{"disambiguationData":[OSD([subQ2,subQ1,subQ0,subQ4])],"isStart":true})]}),makeQuery(id+"F7dXQ7x4IlYUw1S_1.14.F3.opExtrude","CAP_FACE",FACE,{"disambiguationData":[OSD([subQ2,subQ1,subQ0,subQ4])],"isStart":true})]}),makeQuery(id+"F7dXQ7x4IlYUw1S_1.15.F3.opExtrude","CAP_FACE",FACE,{"disambiguationData":[OSD([subQ2,subQ1,subQ0,subQ4])],"isStart":true})]}),makeQuery(id+"F7dXQ7x4IlYUw1S_1.16.F3.opExtrude","CAP_FACE",FACE,{"disambiguationData":[OSD([subQ2,subQ1,subQ0,subQ4])],"isStart":true})]}),makeQuery(id+"F7dXQ7x4IlYUw1S_1.17.F3.opExtrude","CAP_FACE",FACE,{"disambiguationData":[OSD([subQ2,subQ1,subQ0,subQ4])],"isStart":true})]}),makeQuery(id+"F7dXQ7x4IlYUw1S_1.18.F3.opExtrude","CAP_FACE",FACE,{"disambiguationData":[OSD([subQ2,subQ1,subQ0,subQ4])],"isStart":true})]}),makeQuery(id+"F7dXQ7x4IlYUw1S_1.19.F3.opExtrude","CAP_FACE",FACE,{"disambiguationData":[OSD([subQ2,subQ1,subQ0,subQ4])],"isStart":true})]}),makeQuery(id+"F7dXQ7x4IlYUw1S_1.20.F3.opExtrude","CAP_FACE",FACE,{"disambiguationData":[OSD([subQ2,subQ1,subQ0,subQ4])],"isStart":true})]}),makeQuery(id+"F7dXQ7x4IlYUw1S_1.21.F3.opExtrude","CAP_FACE",FACE,{"disambiguationData":[OSD([subQ2,subQ1,subQ0,subQ4])],"isStart":true})]}),makeQuery(id+"F7dXQ7x4IlYUw1S_1.22.F3.opExtrude","CAP_FACE",FACE,{"disambiguationData":[OSD([subQ2,subQ1,subQ0,subQ4])],"isStart":true})]}),makeQuery(id+"F7dXQ7x4IlYUw1S_1.23.F3.opExtrude","CAP_FACE",FACE,{"disambiguationData":[OSD([subQ2,subQ1,subQ0,subQ4])],"isStart":true})]}),makeQuery(id+"F7dXQ7x4IlYUw1S_1.24.F3.opExtrude","CAP_FACE",FACE,{"disambiguationData":[OSD([subQ2,subQ1,subQ0,subQ4])],"isStart":true})]}),makeQuery(id+"F7dXQ7x4IlYUw1S_1.25.F3.opExtrude","CAP_FACE",FACE,{"disambiguationData":[OSD([subQ2,subQ1,subQ0,subQ4])],"isStart":true})]}),makeQuery(id+"F7dXQ7x4IlYUw1S_1.26.F3.opExtrude","CAP_FACE",FACE,{"disambiguationData":[OSD([subQ2,subQ1,subQ0,subQ4])],"isStart":true})]}),makeQuery(id+"F7dXQ7x4IlYUw1S_1.27.F3.opExtrude","CAP_FACE",FACE,{"disambiguationData":[OSD([subQ2,subQ1,subQ0,subQ4])],"isStart":true})]}),makeQuery(id+"F7dXQ7x4IlYUw1S_1.28.F3.opExtrude","CAP_FACE",FACE,{"disambiguationData":[OSD([subQ2,subQ1,subQ0,subQ4])],"isStart":true})]}),makeQuery(id+"F7dXQ7x4IlYUw1S_1.29.F3.opExtrude","CAP_FACE",FACE,{"disambiguationData":[OSD([subQ2,subQ1,subQ0,subQ4])],"isStart":true})]}),makeQuery(id+"F7dXQ7x4IlYUw1S_1.30.F3.opExtrude","CAP_FACE",FACE,{"disambiguationData":[OSD([subQ2,subQ1,subQ0,subQ4])],"isStart":true})]}),makeQuery(id+"F7dXQ7x4IlYUw1S_1.31.F3.opExtrude","CAP_FACE",FACE,{"disambiguationData":[OSD([subQ2,subQ1,subQ0,subQ4])],"isStart":true})]}),makeQuery(id+"F7dXQ7x4IlYUw1S_1.32.F3.opExtrude","CAP_FACE",FACE,{"disambiguationData":[OSD([subQ2,subQ1,subQ0,subQ4])],"isStart":true})]}),makeQuery(id+"F7dXQ7x4IlYUw1S_1.33.F3.opExtrude","CAP_FACE",FACE,{"disambiguationData":[OSD([subQ2,subQ1,subQ0,subQ4])],"isStart":true})]}),makeQuery(id+"F7dXQ7x4IlYUw1S_1.34.F3.opExtrude","CAP_FACE",FACE,{"disambiguationData":[OSD([subQ2,subQ1,subQ0,subQ4])],"isStart":true})]}),makeQuery(id+"F7dXQ7x4IlYUw1S_1.35.F3.opExtrude","CAP_FACE",FACE,{"disambiguationData":[OSD([subQ2,subQ1,subQ0,subQ4])],"isStart":true})]}),makeQuery(id+"F7dXQ7x4IlYUw1S_1.36.F3.opExtrude","CAP_FACE",FACE,{"disambiguationData":[OSD([subQ2,subQ1,subQ0,subQ4])],"isStart":true})]}),makeQuery(id+"F7dXQ7x4IlYUw1S_1.37.F3.opExtrude","CAP_FACE",FACE,{"disambiguationData":[OSD([subQ2,subQ1,subQ0,subQ4])],"isStart":true})]}),makeQuery(id+"F7dXQ7x4IlYUw1S_1.38.F3.opExtrude","CAP_FACE",FACE,{"disambiguationData":[OSD([subQ2,subQ1,subQ0,subQ4])],"isStart":true})]}),makeQuery(id+"F7dXQ7x4IlYUw1S_1.39.F3.opExtrude","CAP_FACE",FACE,{"disambiguationData":[OSD([subQ2,subQ1,subQ0,subQ4])],"isStart":true})]}),makeQuery(id+"F7dXQ7x4IlYUw1S_1.40.F3.opExtrude","CAP_FACE",FACE,{"disambiguationData":[OSD([subQ2,subQ1,subQ0,subQ4])],"isStart":true})]}),makeQuery(id+"F7dXQ7x4IlYUw1S_1.41.F3.opExtrude","CAP_FACE",FACE,{"disambiguationData":[OSD([subQ2,subQ1,subQ0,subQ4])],"isStart":true})]}),makeQuery(id+"F7dXQ7x4IlYUw1S_1.42.F3.opExtrude","CAP_FACE",FACE,{"disambiguationData":[OSD([subQ2,subQ1,subQ0,subQ4])],"isStart":true})]}),makeQuery(id+"F7dXQ7x4IlYUw1S_1.43.F3.opExtrude","CAP_FACE",FACE,{"disambiguationData":[OSD([subQ2,subQ1,subQ0,subQ4])],"isStart":true})]}),makeQuery(id+"F7dXQ7x4IlYUw1S_1.44.F3.opExtrude","CAP_FACE",FACE,{"disambiguationData":[OSD([subQ2,subQ1,subQ0,subQ4])],"isStart":true})]}),makeQuery(id+"F7dXQ7x4IlYUw1S_1.45.F3.opExtrude","CAP_FACE",FACE,{"disambiguationData":[OSD([subQ2,subQ1,subQ0,subQ4])],"isStart":true})]}),makeQuery(id+"F7dXQ7x4IlYUw1S_1.46.F3.opExtrude","CAP_FACE",FACE,{"disambiguationData":[OSD([subQ2,subQ1,subQ0,subQ4])],"isStart":true})]}),makeQuery(id+"F7dXQ7x4IlYUw1S_1.47.F3.opExtrude","CAP_FACE",FACE,{"disambiguationData":[OSD([subQ2,subQ1,subQ0,subQ4])],"isStart":true})]}),makeQuery(id+"F7dXQ7x4IlYUw1S_1.48.F3.opExtrude","CAP_FACE",FACE,{"disambiguationData":[OSD([subQ2,subQ1,subQ0,subQ4])],"isStart":true})]}),makeQuery(id+"F7dXQ7x4IlYUw1S_1.49.F3.opExtrude","CAP_FACE",FACE,{"disambiguationData":[OSD([subQ2,subQ1,subQ0,subQ4])],"isStart":true})]}),makeQuery(id+"F7dXQ7x4IlYUw1S_1.50.F3.opExtrude","CAP_FACE",FACE,{"disambiguationData":[OSD([subQ2,subQ1,subQ0,subQ4])],"isStart":true})]}),makeQuery(id+"F7dXQ7x4IlYUw1S_1.51.F3.opExtrude","CAP_FACE",FACE,{"disambiguationData":[OSD([subQ2,subQ1,subQ0,subQ4])],"isStart":true})]}),makeQuery(id+"F7dXQ7x4IlYUw1S_1.52.F3.opExtrude","CAP_FACE",FACE,{"disambiguationData":[OSD([subQ2,subQ1,subQ0,subQ4])],"isStart":true})]}),makeQuery(id+"F7dXQ7x4IlYUw1S_1.53.F3.opExtrude","CAP_FACE",FACE,{"disambiguationData":[OSD([subQ2,subQ1,subQ0,subQ4])],"isStart":true})]}),makeQuery(id+"F7dXQ7x4IlYUw1S_1.54.F3.opExtrude","CAP_FACE",FACE,{"disambiguationData":[OSD([subQ2,subQ1,subQ0,subQ4])],"isStart":true})]}),makeQuery(id+"F7dXQ7x4IlYUw1S_1.55.F3.opExtrude","CAP_FACE",FACE,{"disambiguationData":[OSD([subQ2,subQ1,subQ0,subQ4])],"isStart":true})]}),makeQuery(id+"F7dXQ7x4IlYUw1S_1.56.F3.opExtrude","CAP_FACE",FACE,{"disambiguationData":[OSD([subQ2,subQ1,subQ0,subQ4])],"isStart":true})]}),makeQuery(id+"F7dXQ7x4IlYUw1S_1.57.F3.opExtrude","CAP_FACE",FACE,{"disambiguationData":[OSD([subQ2,subQ1,subQ0,subQ4])],"isStart":true})]}),makeQuery(id+"F7dXQ7x4IlYUw1S_1.58.F3.opExtrude","CAP_FACE",FACE,{"disambiguationData":[OSD([subQ2,subQ1,subQ0,subQ4])],"isStart":true})]}),makeQuery(id+"F7dXQ7x4IlYUw1S_1.59.F3.opExtrude","CAP_FACE",FACE,{"disambiguationData":[OSD([subQ2,subQ1,subQ0,subQ4])],"isStart":true})]})});}
            var sketch = newSketch(context, id + "F16", { "sketchPlane" : qUnion([Q0])});
            skLineSegment(sketch, "E59", {"start": v(-373.56, -403.67) * mm, "end": v(-466.42, -506.8) * mm});
            skLineSegment(sketch, "E60", {"start": v(-466.42, -506.8) * mm, "end": v(-466.42, -579.95) * mm});
            skLineSegment(sketch, "E61", {"start": v(-466.42, -579.95) * mm, "end": v(-266.42, -579.95) * mm});
            skLineSegment(sketch, "E62", {"start": v(-266.42, -579.95) * mm, "end": v(-230.54, -499.35) * mm});
            skArc(sketch, "E63", {"start": v(-373.56, -403.67) * mm, "mid": v(-305.81, -457.14) * mm, "end": v(-230.54, -499.35) * mm});
            skSolve(sketch);
        }
        {
            var Q0;
            Q0=qSketchRegion(id+"F16",true);
            var Q1;
            {var subQ1=sQuery(id+"F13.wireOp",EDGE,"E58");Q1=makeQuery(id+"F14.boolean.opBoolean","SPLIT",FACE,{"disambiguationData":[TD([makeQuery(id+"F7dXQ7x4IlYUw1S_1.7.F3.opExtrude","SWEPT_FACE",FACE,{"disambiguationData":[OSD([sQuery(id+"F2.wireOp",EDGE,"E3")])]})])],"derivedFrom":makeQuery(id+"F14.opExtrude","CAP_FACE",FACE,{"disambiguationData":[OSD([subQ1])],"isStart":true})});}
            extrude(context, id + "F17", {"entities" : qUnion([Q0]), "operationType" : NewBodyOperationType.ADD, "endBound" : BoundingType.UP_TO_SURFACE, "oppositeDirection" : true, "endBoundEntityFace" : qUnion([Q1]), "depth" : 25 * mm});
        }
        {
            var Q0;
            Q0=makeQuery(id+"F17.opExtrude","SWEPT_FACE",FACE,{"disambiguationData":[OSD([sQuery(id+"F16.wireOp",EDGE,"E60")])]});
            var sketch = newSketch(context, id + "F18", { "sketchPlane" : qUnion([Q0])});
            skLineSegment(sketch, "E64.bottom", {"start": v(0, -543.38) * mm, "end": v(-149.74, -543.38) * mm});
            skLineSegment(sketch, "E64.top", {"start": v(0, -393.64) * mm, "end": v(-149.74, -393.64) * mm});
            skLineSegment(sketch, "E64.left", {"start": v(0, -543.38) * mm, "end": v(0, -393.64) * mm});
            skLineSegment(sketch, "E64.right", {"start": v(-149.74, -543.38) * mm, "end": v(-149.74, -393.64) * mm});
            skSolve(sketch);
        }
        {
            var Q0;
            Q0=qSketchRegion(id+"F18",true);
            var Q1;
            Q1=makeQuery(id+"F7dXQ7x4IlYUw1S_1.8.F3.opExtrude","CAP_VERTEX",VERTEX,{"disambiguationData":[OSD([sQuery(id+"F2.wireOp",EDGE,"E3"),sQuery(id+"F2.wireOp",EDGE,"E6")])],"isStart":true});
            extrude(context, id + "F19", {"entities" : qUnion([Q0]), "operationType" : NewBodyOperationType.REMOVE, "oppositeDirection" : true, "endBoundEntityVertex" : qUnion([Q1]), "depth" : 60 * mm});
        }
        {
            var Q0;
            Q0=makeQuery(id+"F7.opExtrude","CAP_FACE",FACE,{"disambiguationData":[OSD([sQuery(id+"F6.wireOp",EDGE,"E9")])],"isStart":false});
            var sketch = newSketch(context, id + "F20", { "sketchPlane" : qUnion([Q0])});
            skCircle(sketch, "E65", {"center": v(0, 0) * mm, "radius": 80 * mm});
            skSolve(sketch);
        }
        {
            var Q0;
            Q0=qSketchRegion(id+"F20",true);
            extrude(context, id + "F21", {"entities" : qUnion([Q0]), "depth" : 300 * mm});
        }
        {
            var Q0;
            {var subQ0=sQuery(id+"F2.wireOp",EDGE,"E6");var subQ2=sQuery(id+"F2.wireOp",EDGE,"E2");var subQ3=sQuery(id+"F2.wireOp",EDGE,"E3");var subQ4=sQuery(id+"F0.wireOp",EDGE,"E0");var subQ6=sQuery(id+"F2.wireOp",EDGE,"E7");var subQ7=makeQuery(id+"F7dXQ7x4IlYUw1S_1.59.F3.boolean.opBoolean","MERGE",FACE,{"derivedFrom":[makeQuery(id+"F7dXQ7x4IlYUw1S_1.58.F3.boolean.opBoolean","MERGE",FACE,{"derivedFrom":[makeQuery(id+"F7dXQ7x4IlYUw1S_1.57.F3.boolean.opBoolean","MERGE",FACE,{"derivedFrom":[makeQuery(id+"F7dXQ7x4IlYUw1S_1.56.F3.boolean.opBoolean","MERGE",FACE,{"derivedFrom":[makeQuery(id+"F7dXQ7x4IlYUw1S_1.55.F3.boolean.opBoolean","MERGE",FACE,{"derivedFrom":[makeQuery(id+"F7dXQ7x4IlYUw1S_1.54.F3.boolean.opBoolean","MERGE",FACE,{"derivedFrom":[makeQuery(id+"F7dXQ7x4IlYUw1S_1.53.F3.boolean.opBoolean","MERGE",FACE,{"derivedFrom":[makeQuery(id+"F7dXQ7x4IlYUw1S_1.52.F3.boolean.opBoolean","MERGE",FACE,{"derivedFrom":[makeQuery(id+"F7dXQ7x4IlYUw1S_1.51.F3.boolean.opBoolean","MERGE",FACE,{"derivedFrom":[makeQuery(id+"F7dXQ7x4IlYUw1S_1.50.F3.boolean.opBoolean","MERGE",FACE,{"derivedFrom":[makeQuery(id+"F7dXQ7x4IlYUw1S_1.49.F3.boolean.opBoolean","MERGE",FACE,{"derivedFrom":[makeQuery(id+"F7dXQ7x4IlYUw1S_1.48.F3.boolean.opBoolean","MERGE",FACE,{"derivedFrom":[makeQuery(id+"F7dXQ7x4IlYUw1S_1.47.F3.boolean.opBoolean","MERGE",FACE,{"derivedFrom":[makeQuery(id+"F7dXQ7x4IlYUw1S_1.46.F3.boolean.opBoolean","MERGE",FACE,{"derivedFrom":[makeQuery(id+"F7dXQ7x4IlYUw1S_1.45.F3.boolean.opBoolean","MERGE",FACE,{"derivedFrom":[makeQuery(id+"F7dXQ7x4IlYUw1S_1.44.F3.boolean.opBoolean","MERGE",FACE,{"derivedFrom":[makeQuery(id+"F7dXQ7x4IlYUw1S_1.43.F3.boolean.opBoolean","MERGE",FACE,{"derivedFrom":[makeQuery(id+"F7dXQ7x4IlYUw1S_1.42.F3.boolean.opBoolean","MERGE",FACE,{"derivedFrom":[makeQuery(id+"F7dXQ7x4IlYUw1S_1.41.F3.boolean.opBoolean","MERGE",FACE,{"derivedFrom":[makeQuery(id+"F7dXQ7x4IlYUw1S_1.40.F3.boolean.opBoolean","MERGE",FACE,{"derivedFrom":[makeQuery(id+"F7dXQ7x4IlYUw1S_1.39.F3.boolean.opBoolean","MERGE",FACE,{"derivedFrom":[makeQuery(id+"F7dXQ7x4IlYUw1S_1.38.F3.boolean.opBoolean","MERGE",FACE,{"derivedFrom":[makeQuery(id+"F7dXQ7x4IlYUw1S_1.37.F3.boolean.opBoolean","MERGE",FACE,{"derivedFrom":[makeQuery(id+"F7dXQ7x4IlYUw1S_1.36.F3.boolean.opBoolean","MERGE",FACE,{"derivedFrom":[makeQuery(id+"F7dXQ7x4IlYUw1S_1.35.F3.boolean.opBoolean","MERGE",FACE,{"derivedFrom":[makeQuery(id+"F7dXQ7x4IlYUw1S_1.34.F3.boolean.opBoolean","MERGE",FACE,{"derivedFrom":[makeQuery(id+"F7dXQ7x4IlYUw1S_1.33.F3.boolean.opBoolean","MERGE",FACE,{"derivedFrom":[makeQuery(id+"F7dXQ7x4IlYUw1S_1.32.F3.boolean.opBoolean","MERGE",FACE,{"derivedFrom":[makeQuery(id+"F7dXQ7x4IlYUw1S_1.31.F3.boolean.opBoolean","MERGE",FACE,{"derivedFrom":[makeQuery(id+"F7dXQ7x4IlYUw1S_1.30.F3.boolean.opBoolean","MERGE",FACE,{"derivedFrom":[makeQuery(id+"F7dXQ7x4IlYUw1S_1.29.F3.boolean.opBoolean","MERGE",FACE,{"derivedFrom":[makeQuery(id+"F7dXQ7x4IlYUw1S_1.28.F3.boolean.opBoolean","MERGE",FACE,{"derivedFrom":[makeQuery(id+"F7dXQ7x4IlYUw1S_1.27.F3.boolean.opBoolean","MERGE",FACE,{"derivedFrom":[makeQuery(id+"F7dXQ7x4IlYUw1S_1.26.F3.boolean.opBoolean","MERGE",FACE,{"derivedFrom":[makeQuery(id+"F7dXQ7x4IlYUw1S_1.25.F3.boolean.opBoolean","MERGE",FACE,{"derivedFrom":[makeQuery(id+"F7dXQ7x4IlYUw1S_1.24.F3.boolean.opBoolean","MERGE",FACE,{"derivedFrom":[makeQuery(id+"F7dXQ7x4IlYUw1S_1.23.F3.boolean.opBoolean","MERGE",FACE,{"derivedFrom":[makeQuery(id+"F7dXQ7x4IlYUw1S_1.22.F3.boolean.opBoolean","MERGE",FACE,{"derivedFrom":[makeQuery(id+"F7dXQ7x4IlYUw1S_1.21.F3.boolean.opBoolean","MERGE",FACE,{"derivedFrom":[makeQuery(id+"F7dXQ7x4IlYUw1S_1.20.F3.boolean.opBoolean","MERGE",FACE,{"derivedFrom":[makeQuery(id+"F7dXQ7x4IlYUw1S_1.19.F3.boolean.opBoolean","MERGE",FACE,{"derivedFrom":[makeQuery(id+"F7dXQ7x4IlYUw1S_1.18.F3.boolean.opBoolean","MERGE",FACE,{"derivedFrom":[makeQuery(id+"F7dXQ7x4IlYUw1S_1.17.F3.boolean.opBoolean","MERGE",FACE,{"derivedFrom":[makeQuery(id+"F7dXQ7x4IlYUw1S_1.16.F3.boolean.opBoolean","MERGE",FACE,{"derivedFrom":[makeQuery(id+"F7dXQ7x4IlYUw1S_1.15.F3.boolean.opBoolean","MERGE",FACE,{"derivedFrom":[makeQuery(id+"F7dXQ7x4IlYUw1S_1.14.F3.boolean.opBoolean","MERGE",FACE,{"derivedFrom":[makeQuery(id+"F7dXQ7x4IlYUw1S_1.13.F3.boolean.opBoolean","MERGE",FACE,{"derivedFrom":[makeQuery(id+"F7dXQ7x4IlYUw1S_1.12.F3.boolean.opBoolean","MERGE",FACE,{"derivedFrom":[makeQuery(id+"F7dXQ7x4IlYUw1S_1.11.F3.boolean.opBoolean","MERGE",FACE,{"derivedFrom":[makeQuery(id+"F7dXQ7x4IlYUw1S_1.10.F3.boolean.opBoolean","MERGE",FACE,{"derivedFrom":[makeQuery(id+"F7dXQ7x4IlYUw1S_1.9.F3.boolean.opBoolean","MERGE",FACE,{"derivedFrom":[makeQuery(id+"F7dXQ7x4IlYUw1S_1.8.F3.boolean.opBoolean","MERGE",FACE,{"derivedFrom":[makeQuery(id+"F7dXQ7x4IlYUw1S_1.7.F3.boolean.opBoolean","MERGE",FACE,{"derivedFrom":[makeQuery(id+"F7dXQ7x4IlYUw1S_1.6.F3.boolean.opBoolean","MERGE",FACE,{"derivedFrom":[makeQuery(id+"F7dXQ7x4IlYUw1S_1.5.F3.boolean.opBoolean","MERGE",FACE,{"derivedFrom":[makeQuery(id+"F7dXQ7x4IlYUw1S_1.4.F3.boolean.opBoolean","MERGE",FACE,{"derivedFrom":[makeQuery(id+"F7dXQ7x4IlYUw1S_1.3.F3.boolean.opBoolean","MERGE",FACE,{"derivedFrom":[makeQuery(id+"F7dXQ7x4IlYUw1S_1.2.F3.boolean.opBoolean","MERGE",FACE,{"derivedFrom":[makeQuery(id+"F7dXQ7x4IlYUw1S_1.1.F3.boolean.opBoolean","MERGE",FACE,{"derivedFrom":[makeQuery(id+"F3.boolean.opBoolean","MERGE",FACE,{"derivedFrom":[makeQuery(id+"F1.opExtrude","CAP_FACE",FACE,{"disambiguationData":[OSD([subQ4])],"isStart":true}),makeQuery(id+"F3.opExtrude","CAP_FACE",FACE,{"disambiguationData":[OSD([subQ2,subQ3,subQ0,subQ6])],"isStart":true})]}),makeQuery(id+"F7dXQ7x4IlYUw1S_1.1.F3.opExtrude","CAP_FACE",FACE,{"disambiguationData":[OSD([subQ2,subQ3,subQ0,subQ6])],"isStart":true})]}),makeQuery(id+"F7dXQ7x4IlYUw1S_1.2.F3.opExtrude","CAP_FACE",FACE,{"disambiguationData":[OSD([subQ2,subQ3,subQ0,subQ6])],"isStart":true})]}),makeQuery(id+"F7dXQ7x4IlYUw1S_1.3.F3.opExtrude","CAP_FACE",FACE,{"disambiguationData":[OSD([subQ2,subQ3,subQ0,subQ6])],"isStart":true})]}),makeQuery(id+"F7dXQ7x4IlYUw1S_1.4.F3.opExtrude","CAP_FACE",FACE,{"disambiguationData":[OSD([subQ2,subQ3,subQ0,subQ6])],"isStart":true})]}),makeQuery(id+"F7dXQ7x4IlYUw1S_1.5.F3.opExtrude","CAP_FACE",FACE,{"disambiguationData":[OSD([subQ2,subQ3,subQ0,subQ6])],"isStart":true})]}),makeQuery(id+"F7dXQ7x4IlYUw1S_1.6.F3.opExtrude","CAP_FACE",FACE,{"disambiguationData":[OSD([subQ2,subQ3,subQ0,subQ6])],"isStart":true})]}),makeQuery(id+"F7dXQ7x4IlYUw1S_1.7.F3.opExtrude","CAP_FACE",FACE,{"disambiguationData":[OSD([subQ2,subQ3,subQ0,subQ6])],"isStart":true})]}),makeQuery(id+"F7dXQ7x4IlYUw1S_1.8.F3.opExtrude","CAP_FACE",FACE,{"disambiguationData":[OSD([subQ2,subQ3,subQ0,subQ6])],"isStart":true})]}),makeQuery(id+"F7dXQ7x4IlYUw1S_1.9.F3.opExtrude","CAP_FACE",FACE,{"disambiguationData":[OSD([subQ2,subQ3,subQ0,subQ6])],"isStart":true})]}),makeQuery(id+"F7dXQ7x4IlYUw1S_1.10.F3.opExtrude","CAP_FACE",FACE,{"disambiguationData":[OSD([subQ2,subQ3,subQ0,subQ6])],"isStart":true})]}),makeQuery(id+"F7dXQ7x4IlYUw1S_1.11.F3.opExtrude","CAP_FACE",FACE,{"disambiguationData":[OSD([subQ2,subQ3,subQ0,subQ6])],"isStart":true})]}),makeQuery(id+"F7dXQ7x4IlYUw1S_1.12.F3.opExtrude","CAP_FACE",FACE,{"disambiguationData":[OSD([subQ2,subQ3,subQ0,subQ6])],"isStart":true})]}),makeQuery(id+"F7dXQ7x4IlYUw1S_1.13.F3.opExtrude","CAP_FACE",FACE,{"disambiguationData":[OSD([subQ2,subQ3,subQ0,subQ6])],"isStart":true})]}),makeQuery(id+"F7dXQ7x4IlYUw1S_1.14.F3.opExtrude","CAP_FACE",FACE,{"disambiguationData":[OSD([subQ2,subQ3,subQ0,subQ6])],"isStart":true})]}),makeQuery(id+"F7dXQ7x4IlYUw1S_1.15.F3.opExtrude","CAP_FACE",FACE,{"disambiguationData":[OSD([subQ2,subQ3,subQ0,subQ6])],"isStart":true})]}),makeQuery(id+"F7dXQ7x4IlYUw1S_1.16.F3.opExtrude","CAP_FACE",FACE,{"disambiguationData":[OSD([subQ2,subQ3,subQ0,subQ6])],"isStart":true})]}),makeQuery(id+"F7dXQ7x4IlYUw1S_1.17.F3.opExtrude","CAP_FACE",FACE,{"disambiguationData":[OSD([subQ2,subQ3,subQ0,subQ6])],"isStart":true})]}),makeQuery(id+"F7dXQ7x4IlYUw1S_1.18.F3.opExtrude","CAP_FACE",FACE,{"disambiguationData":[OSD([subQ2,subQ3,subQ0,subQ6])],"isStart":true})]}),makeQuery(id+"F7dXQ7x4IlYUw1S_1.19.F3.opExtrude","CAP_FACE",FACE,{"disambiguationData":[OSD([subQ2,subQ3,subQ0,subQ6])],"isStart":true})]}),makeQuery(id+"F7dXQ7x4IlYUw1S_1.20.F3.opExtrude","CAP_FACE",FACE,{"disambiguationData":[OSD([subQ2,subQ3,subQ0,subQ6])],"isStart":true})]}),makeQuery(id+"F7dXQ7x4IlYUw1S_1.21.F3.opExtrude","CAP_FACE",FACE,{"disambiguationData":[OSD([subQ2,subQ3,subQ0,subQ6])],"isStart":true})]}),makeQuery(id+"F7dXQ7x4IlYUw1S_1.22.F3.opExtrude","CAP_FACE",FACE,{"disambiguationData":[OSD([subQ2,subQ3,subQ0,subQ6])],"isStart":true})]}),makeQuery(id+"F7dXQ7x4IlYUw1S_1.23.F3.opExtrude","CAP_FACE",FACE,{"disambiguationData":[OSD([subQ2,subQ3,subQ0,subQ6])],"isStart":true})]}),makeQuery(id+"F7dXQ7x4IlYUw1S_1.24.F3.opExtrude","CAP_FACE",FACE,{"disambiguationData":[OSD([subQ2,subQ3,subQ0,subQ6])],"isStart":true})]}),makeQuery(id+"F7dXQ7x4IlYUw1S_1.25.F3.opExtrude","CAP_FACE",FACE,{"disambiguationData":[OSD([subQ2,subQ3,subQ0,subQ6])],"isStart":true})]}),makeQuery(id+"F7dXQ7x4IlYUw1S_1.26.F3.opExtrude","CAP_FACE",FACE,{"disambiguationData":[OSD([subQ2,subQ3,subQ0,subQ6])],"isStart":true})]}),makeQuery(id+"F7dXQ7x4IlYUw1S_1.27.F3.opExtrude","CAP_FACE",FACE,{"disambiguationData":[OSD([subQ2,subQ3,subQ0,subQ6])],"isStart":true})]}),makeQuery(id+"F7dXQ7x4IlYUw1S_1.28.F3.opExtrude","CAP_FACE",FACE,{"disambiguationData":[OSD([subQ2,subQ3,subQ0,subQ6])],"isStart":true})]}),makeQuery(id+"F7dXQ7x4IlYUw1S_1.29.F3.opExtrude","CAP_FACE",FACE,{"disambiguationData":[OSD([subQ2,subQ3,subQ0,subQ6])],"isStart":true})]}),makeQuery(id+"F7dXQ7x4IlYUw1S_1.30.F3.opExtrude","CAP_FACE",FACE,{"disambiguationData":[OSD([subQ2,subQ3,subQ0,subQ6])],"isStart":true})]}),makeQuery(id+"F7dXQ7x4IlYUw1S_1.31.F3.opExtrude","CAP_FACE",FACE,{"disambiguationData":[OSD([subQ2,subQ3,subQ0,subQ6])],"isStart":true})]}),makeQuery(id+"F7dXQ7x4IlYUw1S_1.32.F3.opExtrude","CAP_FACE",FACE,{"disambiguationData":[OSD([subQ2,subQ3,subQ0,subQ6])],"isStart":true})]}),makeQuery(id+"F7dXQ7x4IlYUw1S_1.33.F3.opExtrude","CAP_FACE",FACE,{"disambiguationData":[OSD([subQ2,subQ3,subQ0,subQ6])],"isStart":true})]}),makeQuery(id+"F7dXQ7x4IlYUw1S_1.34.F3.opExtrude","CAP_FACE",FACE,{"disambiguationData":[OSD([subQ2,subQ3,subQ0,subQ6])],"isStart":true})]}),makeQuery(id+"F7dXQ7x4IlYUw1S_1.35.F3.opExtrude","CAP_FACE",FACE,{"disambiguationData":[OSD([subQ2,subQ3,subQ0,subQ6])],"isStart":true})]}),makeQuery(id+"F7dXQ7x4IlYUw1S_1.36.F3.opExtrude","CAP_FACE",FACE,{"disambiguationData":[OSD([subQ2,subQ3,subQ0,subQ6])],"isStart":true})]}),makeQuery(id+"F7dXQ7x4IlYUw1S_1.37.F3.opExtrude","CAP_FACE",FACE,{"disambiguationData":[OSD([subQ2,subQ3,subQ0,subQ6])],"isStart":true})]}),makeQuery(id+"F7dXQ7x4IlYUw1S_1.38.F3.opExtrude","CAP_FACE",FACE,{"disambiguationData":[OSD([subQ2,subQ3,subQ0,subQ6])],"isStart":true})]}),makeQuery(id+"F7dXQ7x4IlYUw1S_1.39.F3.opExtrude","CAP_FACE",FACE,{"disambiguationData":[OSD([subQ2,subQ3,subQ0,subQ6])],"isStart":true})]}),makeQuery(id+"F7dXQ7x4IlYUw1S_1.40.F3.opExtrude","CAP_FACE",FACE,{"disambiguationData":[OSD([subQ2,subQ3,subQ0,subQ6])],"isStart":true})]}),makeQuery(id+"F7dXQ7x4IlYUw1S_1.41.F3.opExtrude","CAP_FACE",FACE,{"disambiguationData":[OSD([subQ2,subQ3,subQ0,subQ6])],"isStart":true})]}),makeQuery(id+"F7dXQ7x4IlYUw1S_1.42.F3.opExtrude","CAP_FACE",FACE,{"disambiguationData":[OSD([subQ2,subQ3,subQ0,subQ6])],"isStart":true})]}),makeQuery(id+"F7dXQ7x4IlYUw1S_1.43.F3.opExtrude","CAP_FACE",FACE,{"disambiguationData":[OSD([subQ2,subQ3,subQ0,subQ6])],"isStart":true})]}),makeQuery(id+"F7dXQ7x4IlYUw1S_1.44.F3.opExtrude","CAP_FACE",FACE,{"disambiguationData":[OSD([subQ2,subQ3,subQ0,subQ6])],"isStart":true})]}),makeQuery(id+"F7dXQ7x4IlYUw1S_1.45.F3.opExtrude","CAP_FACE",FACE,{"disambiguationData":[OSD([subQ2,subQ3,subQ0,subQ6])],"isStart":true})]}),makeQuery(id+"F7dXQ7x4IlYUw1S_1.46.F3.opExtrude","CAP_FACE",FACE,{"disambiguationData":[OSD([subQ2,subQ3,subQ0,subQ6])],"isStart":true})]}),makeQuery(id+"F7dXQ7x4IlYUw1S_1.47.F3.opExtrude","CAP_FACE",FACE,{"disambiguationData":[OSD([subQ2,subQ3,subQ0,subQ6])],"isStart":true})]}),makeQuery(id+"F7dXQ7x4IlYUw1S_1.48.F3.opExtrude","CAP_FACE",FACE,{"disambiguationData":[OSD([subQ2,subQ3,subQ0,subQ6])],"isStart":true})]}),makeQuery(id+"F7dXQ7x4IlYUw1S_1.49.F3.opExtrude","CAP_FACE",FACE,{"disambiguationData":[OSD([subQ2,subQ3,subQ0,subQ6])],"isStart":true})]}),makeQuery(id+"F7dXQ7x4IlYUw1S_1.50.F3.opExtrude","CAP_FACE",FACE,{"disambiguationData":[OSD([subQ2,subQ3,subQ0,subQ6])],"isStart":true})]}),makeQuery(id+"F7dXQ7x4IlYUw1S_1.51.F3.opExtrude","CAP_FACE",FACE,{"disambiguationData":[OSD([subQ2,subQ3,subQ0,subQ6])],"isStart":true})]}),makeQuery(id+"F7dXQ7x4IlYUw1S_1.52.F3.opExtrude","CAP_FACE",FACE,{"disambiguationData":[OSD([subQ2,subQ3,subQ0,subQ6])],"isStart":true})]}),makeQuery(id+"F7dXQ7x4IlYUw1S_1.53.F3.opExtrude","CAP_FACE",FACE,{"disambiguationData":[OSD([subQ2,subQ3,subQ0,subQ6])],"isStart":true})]}),makeQuery(id+"F7dXQ7x4IlYUw1S_1.54.F3.opExtrude","CAP_FACE",FACE,{"disambiguationData":[OSD([subQ2,subQ3,subQ0,subQ6])],"isStart":true})]}),makeQuery(id+"F7dXQ7x4IlYUw1S_1.55.F3.opExtrude","CAP_FACE",FACE,{"disambiguationData":[OSD([subQ2,subQ3,subQ0,subQ6])],"isStart":true})]}),makeQuery(id+"F7dXQ7x4IlYUw1S_1.56.F3.opExtrude","CAP_FACE",FACE,{"disambiguationData":[OSD([subQ2,subQ3,subQ0,subQ6])],"isStart":true})]}),makeQuery(id+"F7dXQ7x4IlYUw1S_1.57.F3.opExtrude","CAP_FACE",FACE,{"disambiguationData":[OSD([subQ2,subQ3,subQ0,subQ6])],"isStart":true})]}),makeQuery(id+"F7dXQ7x4IlYUw1S_1.58.F3.opExtrude","CAP_FACE",FACE,{"disambiguationData":[OSD([subQ2,subQ3,subQ0,subQ6])],"isStart":true})]}),makeQuery(id+"F7dXQ7x4IlYUw1S_1.59.F3.opExtrude","CAP_FACE",FACE,{"disambiguationData":[OSD([subQ2,subQ3,subQ0,subQ6])],"isStart":true})]});Q0=makeQuery(id+"FgvlKzndbuIrR9h_1.1.F17.boolean.opBoolean","MERGE",FACE,{"derivedFrom":[makeQuery(id+"F5.boolean.opBoolean","SPLIT",FACE,{"disambiguationData":[TD([makeQuery(id+"F7dXQ7x4IlYUw1S_1.19.F3.opExtrude","SWEPT_FACE",FACE,{"disambiguationData":[OSD([subQ2])]})])],"derivedFrom":subQ7}),makeQuery(id+"F5.boolean.opBoolean","SPLIT",FACE,{"disambiguationData":[TD([makeQuery(id+"F7dXQ7x4IlYUw1S_1.20.F3.opExtrude","SWEPT_FACE",FACE,{"disambiguationData":[OSD([subQ2])]})])],"derivedFrom":subQ7}),makeQuery(id+"F5.boolean.opBoolean","SPLIT",FACE,{"disambiguationData":[TD([makeQuery(id+"F7dXQ7x4IlYUw1S_1.21.F3.opExtrude","SWEPT_FACE",FACE,{"disambiguationData":[OSD([subQ2])]})])],"derivedFrom":subQ7}),makeQuery(id+"F5.boolean.opBoolean","SPLIT",FACE,{"disambiguationData":[TD([makeQuery(id+"F7dXQ7x4IlYUw1S_1.22.F3.opExtrude","SWEPT_FACE",FACE,{"disambiguationData":[OSD([subQ2])]})])],"derivedFrom":subQ7}),makeQuery(id+"FgvlKzndbuIrR9h_1.1.F17.opExtrude","CAP_FACE",FACE,{"disambiguationData":[OSD([sQuery(id+"F16.wireOp",EDGE,"E59"),sQuery(id+"F16.wireOp",EDGE,"E60"),sQuery(id+"F16.wireOp",EDGE,"E61"),sQuery(id+"F16.wireOp",EDGE,"E62"),sQuery(id+"F16.wireOp",EDGE,"E63")])],"isStart":true})]});}
            var sketch = newSketch(context, id + "F22", { "sketchPlane" : qUnion([Q0])});
            skLineSegment(sketch, "E66", {"start": v(-466.42, -579.95) * mm, "end": v(-266.42, -579.95) * mm});
            skLineSegment(sketch, "E67", {"start": v(-266.42, -579.95) * mm, "end": v(-270.33, -588.73) * mm});
            skLineSegment(sketch, "E68", {"start": v(-270.33, -588.73) * mm, "end": v(-466.42, -588.73) * mm});
            skLineSegment(sketch, "E69", {"start": v(-466.42, -588.73) * mm, "end": v(-466.42, -579.95) * mm});
            skLineSegment(sketch, "E70", {"start": v(266.42, -579.95) * mm, "end": v(466.42, -579.95) * mm});
            skLineSegment(sketch, "E71", {"start": v(466.42, -579.95) * mm, "end": v(466.42, -588.73) * mm});
            skLineSegment(sketch, "E72", {"start": v(466.42, -588.73) * mm, "end": v(270.33, -588.73) * mm});
            skLineSegment(sketch, "E73", {"start": v(270.33, -588.73) * mm, "end": v(266.42, -579.95) * mm});
            skSolve(sketch);
        }
        {
            var Q0;
            Q0=qSketchRegion(id+"F22",true);
            var Q1;
            Q1=makeQuery(id+"F17.opExtrude","CAP_FACE",FACE,{"disambiguationData":[OSD([sQuery(id+"F16.wireOp",EDGE,"E59"),sQuery(id+"F16.wireOp",EDGE,"E60"),sQuery(id+"F16.wireOp",EDGE,"E61"),sQuery(id+"F16.wireOp",EDGE,"E62"),sQuery(id+"F16.wireOp",EDGE,"E63")])],"isStart":false});
            extrude(context, id + "F23", {"entities" : qUnion([Q0]), "operationType" : NewBodyOperationType.ADD, "endBound" : BoundingType.UP_TO_SURFACE, "oppositeDirection" : true, "endBoundEntityFace" : qUnion([Q1]), "depth" : 25 * mm});
        }
        {
            var Q0;
            Q0=makeQuery(id+"F21.opExtrude","CAP_FACE",FACE,{"disambiguationData":[OSD([sQuery(id+"F20.wireOp",EDGE,"E65")])],"isStart":false});
            cPlane(context, id + "F24", {"entities" : qUnion([Q0]), "cplaneType" : CPlaneType.OFFSET, "offset" : 10 * mm, "oppositeDirection" : true, "width" : 150 * mm, "height" : 150 * mm});
        }
        {
            var Q0;
            Q0=qCreatedBy(id+"F24.planeOp",FACE);
            var sketch = newSketch(context, id + "F25", { "sketchPlane" : qUnion([Q0])});
            skCircle(sketch, "E74.0", {"center": v(0, 0) * mm, "radius": 80 * mm});
            skCircle(sketch, "E75", {"center": v(0, 0) * mm, "radius": 207.5 * mm});
            skSolve(sketch);
        }
        {
            var Q0;
            Q0=qSketchRegion(id+"F25",true);
            extrude(context, id + "F26", {"entities" : qUnion([Q0]), "operationType" : NewBodyOperationType.ADD, "oppositeDirection" : true, "depth" : 50 * mm});
        }
        {
            var Q0;
            Q0=makeQuery(id+"F14.opExtrude","CAP_FACE",FACE,{"disambiguationData":[OSD([sQuery(id+"F13.wireOp",EDGE,"E58")])],"isStart":false});
            var sketch = newSketch(context, id + "F27", { "sketchPlane" : qUnion([Q0])});
            skArc(sketch, "E76", {"start": v(-208.82, 508.82) * mm, "mid": v(-388.9, 388.9) * mm, "end": v(-508.82, 208.82) * mm});
            skArc(sketch, "E77", {"start": v(508.82, 208.82) * mm, "mid": v(388.9, 388.9) * mm, "end": v(208.82, 508.82) * mm});
            skArc(sketch, "E78", {"start": v(-508.82, -208.82) * mm, "mid": v(-388.9, -388.9) * mm, "end": v(-208.82, -508.82) * mm});
            skArc(sketch, "E79", {"start": v(208.82, -508.82) * mm, "mid": v(388.9, -388.9) * mm, "end": v(508.82, -208.82) * mm});
            skLineSegment(sketch, "E80", {"start": v(-208.82, 508.82) * mm, "end": v(-208.82, 208.82) * mm});
            skLineSegment(sketch, "E81", {"start": v(-208.82, 208.82) * mm, "end": v(-508.82, 208.82) * mm});
            skLineSegment(sketch, "E82", {"start": v(508.82, 208.82) * mm, "end": v(208.82, 208.82) * mm});
            skLineSegment(sketch, "E83", {"start": v(208.82, 508.82) * mm, "end": v(208.82, 208.82) * mm});
            skLineSegment(sketch, "E84", {"start": v(508.82, -208.82) * mm, "end": v(208.82, -208.82) * mm});
            skLineSegment(sketch, "E85", {"start": v(208.82, -508.82) * mm, "end": v(208.82, -208.82) * mm});
            skLineSegment(sketch, "E86", {"start": v(-208.82, -508.82) * mm, "end": v(-208.82, -208.82) * mm});
            skLineSegment(sketch, "E87", {"start": v(-508.82, -208.82) * mm, "end": v(-208.82, -208.82) * mm});
            skLineSegment(sketch, "E88", {"start": v(-148.82, 208.82) * mm, "end": v(-111.71, 208.82) * mm});
            skLineSegment(sketch, "E89", {"start": v(148.82, 208.82) * mm, "end": v(148.82, 529.48) * mm});
            skLineSegment(sketch, "E90", {"start": v(-148.82, 208.82) * mm, "end": v(-148.82, 529.48) * mm});
            skLineSegment(sketch, "E91", {"start": v(-208.82, 148.82) * mm, "end": v(-208.82, 111.71) * mm});
            skLineSegment(sketch, "E92", {"start": v(-208.82, -148.82) * mm, "end": v(-529.48, -148.82) * mm});
            skLineSegment(sketch, "E93", {"start": v(-208.82, 148.82) * mm, "end": v(-529.48, 148.82) * mm});
            skArc(sketch, "E94", {"start": v(-529.48, 148.82) * mm, "mid": v(-534.33, 130.34) * mm, "end": v(-538.54, 111.71) * mm});
            skArc(sketch, "E95", {"start": v(148.82, 529.48) * mm, "mid": v(130.34, 534.33) * mm, "end": v(111.71, 538.54) * mm});
            skLineSegment(sketch, "E96.bottom", {"start": v(-148.82, 148.82) * mm, "end": v(-127.6, 148.82) * mm});
            skLineSegment(sketch, "E96.top", {"start": v(-148.82, -148.82) * mm, "end": v(-127.6, -148.82) * mm});
            skLineSegment(sketch, "E96.left", {"start": v(-148.82, 148.82) * mm, "end": v(-148.82, 127.6) * mm});
            skLineSegment(sketch, "E96.right", {"start": v(148.82, 148.82) * mm, "end": v(148.82, 127.6) * mm});
            skPoint(sketch, "E97.endSnap0", {"position": v(0, 208.82) * mm});
            skLineSegment(sketch, "E98", {"start": v(-111.71, 538.54) * mm, "end": v(-111.71, 208.82) * mm});
            skLineSegment(sketch, "E99", {"start": v(-96.71, 541.43) * mm, "end": v(-96.71, 208.82) * mm});
            skLineSegment(sketch, "E100", {"start": v(-59.6, 208.82) * mm, "end": v(-59.6, 546.76) * mm});
            skLineSegment(sketch, "E101", {"start": v(-44.6, 548.19) * mm, "end": v(-44.6, 208.82) * mm});
            skLineSegment(sketch, "E102", {"start": v(-7.5, 208.82) * mm, "end": v(-7.5, 549.95) * mm});
            skLineSegment(sketch, "E103", {"start": v(7.5, 549.95) * mm, "end": v(7.5, 208.82) * mm});
            skLineSegment(sketch, "E104", {"start": v(44.6, 548.19) * mm, "end": v(44.6, 208.82) * mm});
            skLineSegment(sketch, "E105", {"start": v(59.6, 208.82) * mm, "end": v(59.6, 546.76) * mm});
            skLineSegment(sketch, "E106", {"start": v(96.71, 541.43) * mm, "end": v(96.71, 208.82) * mm});
            skLineSegment(sketch, "E107", {"start": v(111.71, 208.82) * mm, "end": v(111.71, 538.54) * mm});
            skLineSegment(sketch, "E108.trimOffspring", {"start": v(111.71, 208.82) * mm, "end": v(148.82, 208.82) * mm});
            skLineSegment(sketch, "E109.trimOffspring", {"start": v(59.6, 208.82) * mm, "end": v(96.71, 208.82) * mm});
            skLineSegment(sketch, "E110.trimOffspring", {"start": v(7.5, 208.82) * mm, "end": v(44.6, 208.82) * mm});
            skLineSegment(sketch, "E111.trimOffspring", {"start": v(-44.6, 208.82) * mm, "end": v(-7.5, 208.82) * mm});
            skLineSegment(sketch, "E112.trimOffspring", {"start": v(-96.71, 208.82) * mm, "end": v(-59.6, 208.82) * mm});
            skArc(sketch, "E113.trimOffspring", {"start": v(-111.71, 538.54) * mm, "mid": v(-130.34, 534.33) * mm, "end": v(-148.82, 529.48) * mm});
            skArc(sketch, "E114.trimOffspring", {"start": v(-59.6, 546.76) * mm, "mid": v(-78.2, 544.41) * mm, "end": v(-96.71, 541.43) * mm});
            skArc(sketch, "E115.trimOffspring", {"start": v(-7.5, 549.95) * mm, "mid": v(-26.07, 549.38) * mm, "end": v(-44.6, 548.19) * mm});
            skArc(sketch, "E116.trimOffspring", {"start": v(44.6, 548.19) * mm, "mid": v(26.07, 549.38) * mm, "end": v(7.5, 549.95) * mm});
            skArc(sketch, "E117.trimOffspring", {"start": v(96.71, 541.43) * mm, "mid": v(78.2, 544.41) * mm, "end": v(59.6, 546.76) * mm});
            skLineSegment(sketch, "E118", {"start": v(-58.12, 0) * mm, "end": v(58.12, 0) * mm, "construction": true});
            skLineSegment(sketch, "E119", {"start": v(0, 52.15) * mm, "end": v(0, -52.15) * mm, "construction": true});
            skLineSegment(sketch, "E120", {"start": v(-208.82, 111.71) * mm, "end": v(-538.54, 111.71) * mm});
            skLineSegment(sketch, "E121", {"start": v(-208.82, 96.71) * mm, "end": v(-541.43, 96.71) * mm});
            skLineSegment(sketch, "E122", {"start": v(-208.82, 59.6) * mm, "end": v(-546.76, 59.6) * mm});
            skLineSegment(sketch, "E123", {"start": v(-208.82, 44.6) * mm, "end": v(-548.19, 44.6) * mm});
            skLineSegment(sketch, "E124", {"start": v(-208.82, 7.5) * mm, "end": v(-549.95, 7.5) * mm});
            skLineSegment(sketch, "E125", {"start": v(-208.82, -7.5) * mm, "end": v(-549.95, -7.5) * mm});
            skLineSegment(sketch, "E126", {"start": v(-208.82, -44.6) * mm, "end": v(-548.19, -44.6) * mm});
            skLineSegment(sketch, "E127", {"start": v(-208.82, -96.71) * mm, "end": v(-541.43, -96.71) * mm});
            skLineSegment(sketch, "E128", {"start": v(-208.82, -111.71) * mm, "end": v(-538.54, -111.71) * mm});
            skLineSegment(sketch, "E129", {"start": v(-208.82, -59.6) * mm, "end": v(-546.76, -59.6) * mm});
            skLineSegment(sketch, "E130.trimOffspring", {"start": v(-208.82, 96.71) * mm, "end": v(-208.82, 59.6) * mm});
            skLineSegment(sketch, "E131.trimOffspring", {"start": v(-208.82, 44.6) * mm, "end": v(-208.82, 7.5) * mm});
            skLineSegment(sketch, "E132.trimOffspring", {"start": v(-208.82, -7.5) * mm, "end": v(-208.82, -44.6) * mm});
            skLineSegment(sketch, "E133.trimOffspring", {"start": v(-208.82, -59.6) * mm, "end": v(-208.82, -96.71) * mm});
            skLineSegment(sketch, "E134.trimOffspring", {"start": v(-208.82, -111.71) * mm, "end": v(-208.82, -148.82) * mm});
            skArc(sketch, "E135.trimOffspring", {"start": v(-538.54, -111.71) * mm, "mid": v(-534.33, -130.34) * mm, "end": v(-529.48, -148.82) * mm});
            skArc(sketch, "E136.trimOffspring", {"start": v(-546.76, -59.6) * mm, "mid": v(-544.41, -78.2) * mm, "end": v(-541.43, -96.71) * mm});
            skArc(sketch, "E137.trimOffspring", {"start": v(-549.95, -7.5) * mm, "mid": v(-549.38, -26.07) * mm, "end": v(-548.19, -44.6) * mm});
            skArc(sketch, "E138.trimOffspring", {"start": v(-548.19, 44.6) * mm, "mid": v(-549.38, 26.07) * mm, "end": v(-549.95, 7.5) * mm});
            skArc(sketch, "E139.trimOffspring", {"start": v(-541.43, 96.71) * mm, "mid": v(-544.41, 78.2) * mm, "end": v(-546.76, 59.6) * mm});
            skLineSegment(sketch, "E140.MirrorCS", {"start": v(208.82, 96.71) * mm, "end": v(208.82, 59.6) * mm});
            skArc(sketch, "E141.MirrorCS", {"start": v(548.19, 44.6) * mm, "mid": v(549.38, 26.07) * mm, "end": v(549.95, 7.5) * mm});
            skArc(sketch, "E142.MirrorCS", {"start": v(538.54, -111.71) * mm, "mid": v(534.33, -130.34) * mm, "end": v(529.48, -148.82) * mm});
            skArc(sketch, "E143.MirrorCS", {"start": v(529.48, 148.82) * mm, "mid": v(534.33, 130.34) * mm, "end": v(538.54, 111.71) * mm});
            skLineSegment(sketch, "E144.MirrorCS", {"start": v(208.82, 148.82) * mm, "end": v(208.82, 111.71) * mm});
            skLineSegment(sketch, "E145.MirrorCS", {"start": v(208.82, -59.6) * mm, "end": v(208.82, -96.71) * mm});
            skArc(sketch, "E146.MirrorCS", {"start": v(549.95, -7.5) * mm, "mid": v(549.38, -26.07) * mm, "end": v(548.19, -44.6) * mm});
            skLineSegment(sketch, "E147.MirrorCS", {"start": v(208.82, 44.6) * mm, "end": v(208.82, 7.5) * mm});
            skArc(sketch, "E148.MirrorCS", {"start": v(546.76, -59.6) * mm, "mid": v(544.41, -78.2) * mm, "end": v(541.43, -96.71) * mm});
            skLineSegment(sketch, "E149.MirrorCS", {"start": v(208.82, -7.5) * mm, "end": v(208.82, -44.6) * mm});
            skLineSegment(sketch, "E150.MirrorCS", {"start": v(208.82, -111.71) * mm, "end": v(208.82, -148.82) * mm});
            skArc(sketch, "E151.MirrorCS", {"start": v(541.43, 96.71) * mm, "mid": v(544.41, 78.2) * mm, "end": v(546.76, 59.6) * mm});
            skLineSegment(sketch, "E152.MirrorCS", {"start": v(208.82, 111.71) * mm, "end": v(538.54, 111.71) * mm});
            skLineSegment(sketch, "E153.MirrorCS", {"start": v(208.82, -44.6) * mm, "end": v(548.19, -44.6) * mm});
            skLineSegment(sketch, "E154.MirrorCS", {"start": v(208.82, 44.6) * mm, "end": v(548.19, 44.6) * mm});
            skLineSegment(sketch, "E155.MirrorCS", {"start": v(208.82, 7.5) * mm, "end": v(549.95, 7.5) * mm});
            skLineSegment(sketch, "E156.MirrorCS", {"start": v(208.82, 59.6) * mm, "end": v(546.76, 59.6) * mm});
            skLineSegment(sketch, "E157.MirrorCS", {"start": v(208.82, -111.71) * mm, "end": v(538.54, -111.71) * mm});
            skLineSegment(sketch, "E158.MirrorCS", {"start": v(208.82, -148.82) * mm, "end": v(529.48, -148.82) * mm});
            skLineSegment(sketch, "E159.MirrorCS", {"start": v(208.82, -7.5) * mm, "end": v(549.95, -7.5) * mm});
            skLineSegment(sketch, "E160.MirrorCS", {"start": v(208.82, -96.71) * mm, "end": v(541.43, -96.71) * mm});
            skLineSegment(sketch, "E161.MirrorCS", {"start": v(208.82, 96.71) * mm, "end": v(541.43, 96.71) * mm});
            skLineSegment(sketch, "E162.MirrorCS", {"start": v(208.82, -59.6) * mm, "end": v(546.76, -59.6) * mm});
            skLineSegment(sketch, "E163.MirrorCS", {"start": v(208.82, 148.82) * mm, "end": v(529.48, 148.82) * mm});
            skArc(sketch, "E164.MirrorCS", {"start": v(-7.5, -549.95) * mm, "mid": v(-26.07, -549.38) * mm, "end": v(-44.6, -548.19) * mm});
            skArc(sketch, "E165.MirrorCS", {"start": v(96.71, -541.43) * mm, "mid": v(78.2, -544.41) * mm, "end": v(59.6, -546.76) * mm});
            skLineSegment(sketch, "E166.MirrorCS", {"start": v(59.6, -208.82) * mm, "end": v(96.71, -208.82) * mm});
            skLineSegment(sketch, "E167.MirrorCS", {"start": v(-96.71, -208.82) * mm, "end": v(-59.6, -208.82) * mm});
            skLineSegment(sketch, "E168.MirrorCS", {"start": v(-148.82, -208.82) * mm, "end": v(-111.71, -208.82) * mm});
            skLineSegment(sketch, "E169.MirrorCS", {"start": v(-44.6, -208.82) * mm, "end": v(-7.5, -208.82) * mm});
            skArc(sketch, "E170.MirrorCS", {"start": v(148.82, -529.48) * mm, "mid": v(130.34, -534.33) * mm, "end": v(111.71, -538.54) * mm});
            skArc(sketch, "E171.MirrorCS", {"start": v(-59.6, -546.76) * mm, "mid": v(-78.2, -544.41) * mm, "end": v(-96.71, -541.43) * mm});
            skArc(sketch, "E172.MirrorCS", {"start": v(-111.71, -538.54) * mm, "mid": v(-130.34, -534.33) * mm, "end": v(-148.82, -529.48) * mm});
            skLineSegment(sketch, "E173.MirrorCS", {"start": v(7.5, -208.82) * mm, "end": v(44.6, -208.82) * mm});
            skArc(sketch, "E174.MirrorCS", {"start": v(44.6, -548.19) * mm, "mid": v(26.07, -549.38) * mm, "end": v(7.5, -549.95) * mm});
            skLineSegment(sketch, "E175.MirrorCS", {"start": v(111.71, -208.82) * mm, "end": v(148.82, -208.82) * mm});
            skLineSegment(sketch, "E176.MirrorCS", {"start": v(-59.6, -208.82) * mm, "end": v(-59.6, -546.76) * mm});
            skLineSegment(sketch, "E177.MirrorCS", {"start": v(-96.71, -541.43) * mm, "end": v(-96.71, -208.82) * mm});
            skLineSegment(sketch, "E178.MirrorCS", {"start": v(148.82, -208.82) * mm, "end": v(148.82, -529.48) * mm});
            skLineSegment(sketch, "E179.MirrorCS", {"start": v(-148.82, -208.82) * mm, "end": v(-148.82, -529.48) * mm});
            skLineSegment(sketch, "E180.MirrorCS", {"start": v(59.6, -208.82) * mm, "end": v(59.6, -546.76) * mm});
            skLineSegment(sketch, "E181.MirrorCS", {"start": v(-44.6, -548.19) * mm, "end": v(-44.6, -208.82) * mm});
            skLineSegment(sketch, "E182.MirrorCS", {"start": v(96.71, -541.43) * mm, "end": v(96.71, -208.82) * mm});
            skLineSegment(sketch, "E183.MirrorCS", {"start": v(7.5, -549.95) * mm, "end": v(7.5, -208.82) * mm});
            skLineSegment(sketch, "E184.MirrorCS", {"start": v(44.6, -548.19) * mm, "end": v(44.6, -208.82) * mm});
            skLineSegment(sketch, "E185.MirrorCS", {"start": v(111.71, -208.82) * mm, "end": v(111.71, -538.54) * mm});
            skPoint(sketch, "E186.MirrorP", {"position": v(0, -208.82) * mm});
            skLineSegment(sketch, "E187.MirrorCS", {"start": v(-7.5, -208.82) * mm, "end": v(-7.5, -549.95) * mm});
            skLineSegment(sketch, "E188.MirrorCS", {"start": v(-111.71, -538.54) * mm, "end": v(-111.71, -208.82) * mm});
            skLineSegment(sketch, "E189", {"start": v(-148.82, 127.6) * mm, "end": v(-55.58, 34.37) * mm});
            skLineSegment(sketch, "E190", {"start": v(-127.6, 148.82) * mm, "end": v(-34.37, 55.58) * mm});
            skLineSegment(sketch, "E191", {"start": v(127.6, 148.82) * mm, "end": v(34.37, 55.58) * mm});
            skLineSegment(sketch, "E192", {"start": v(148.82, 127.6) * mm, "end": v(55.58, 34.37) * mm});
            skLineSegment(sketch, "E193", {"start": v(-148.82, -127.6) * mm, "end": v(-55.58, -34.37) * mm});
            skLineSegment(sketch, "E194", {"start": v(-127.6, -148.82) * mm, "end": v(-34.37, -55.58) * mm});
            skLineSegment(sketch, "E195", {"start": v(127.6, -148.82) * mm, "end": v(34.37, -55.58) * mm});
            skLineSegment(sketch, "E196", {"start": v(148.82, -127.6) * mm, "end": v(55.58, -34.37) * mm});
            skLineSegment(sketch, "E197", {"start": v(-55.58, -34.37) * mm, "end": v(-34.37, -55.58) * mm});
            skLineSegment(sketch, "E198", {"start": v(34.37, -55.58) * mm, "end": v(55.58, -34.37) * mm});
            skLineSegment(sketch, "E199", {"start": v(55.58, 34.37) * mm, "end": v(34.37, 55.58) * mm});
            skLineSegment(sketch, "E200", {"start": v(-34.37, 55.58) * mm, "end": v(-55.58, 34.37) * mm});
            skLineSegment(sketch, "E201.trimOffspring", {"start": v(127.6, 148.82) * mm, "end": v(148.82, 148.82) * mm});
            skLineSegment(sketch, "E202.trimOffspring", {"start": v(-148.82, -127.6) * mm, "end": v(-148.82, -148.82) * mm});
            skLineSegment(sketch, "E203.trimOffspring", {"start": v(148.82, -127.6) * mm, "end": v(148.82, -148.82) * mm});
            skLineSegment(sketch, "E204.trimOffspring", {"start": v(127.6, -148.82) * mm, "end": v(148.82, -148.82) * mm});
            skSolve(sketch);
        }
        {
            var Q0;
            Q0=qSketchRegion(id+"F27",true);
            extrude(context, id + "F28", {"entities" : qUnion([Q0]), "operationType" : NewBodyOperationType.REMOVE, "oppositeDirection" : true, "depth" : 10 * mm});
        }
        {
            var Q0;
            Q0=qSketchRegion(id+"F27",true);
            extrude(context, id + "F29", {"entities" : qUnion([Q0]), "operationType" : NewBodyOperationType.REMOVE, "oppositeDirection" : true, "depth" : 25 * mm});
        }
    });
